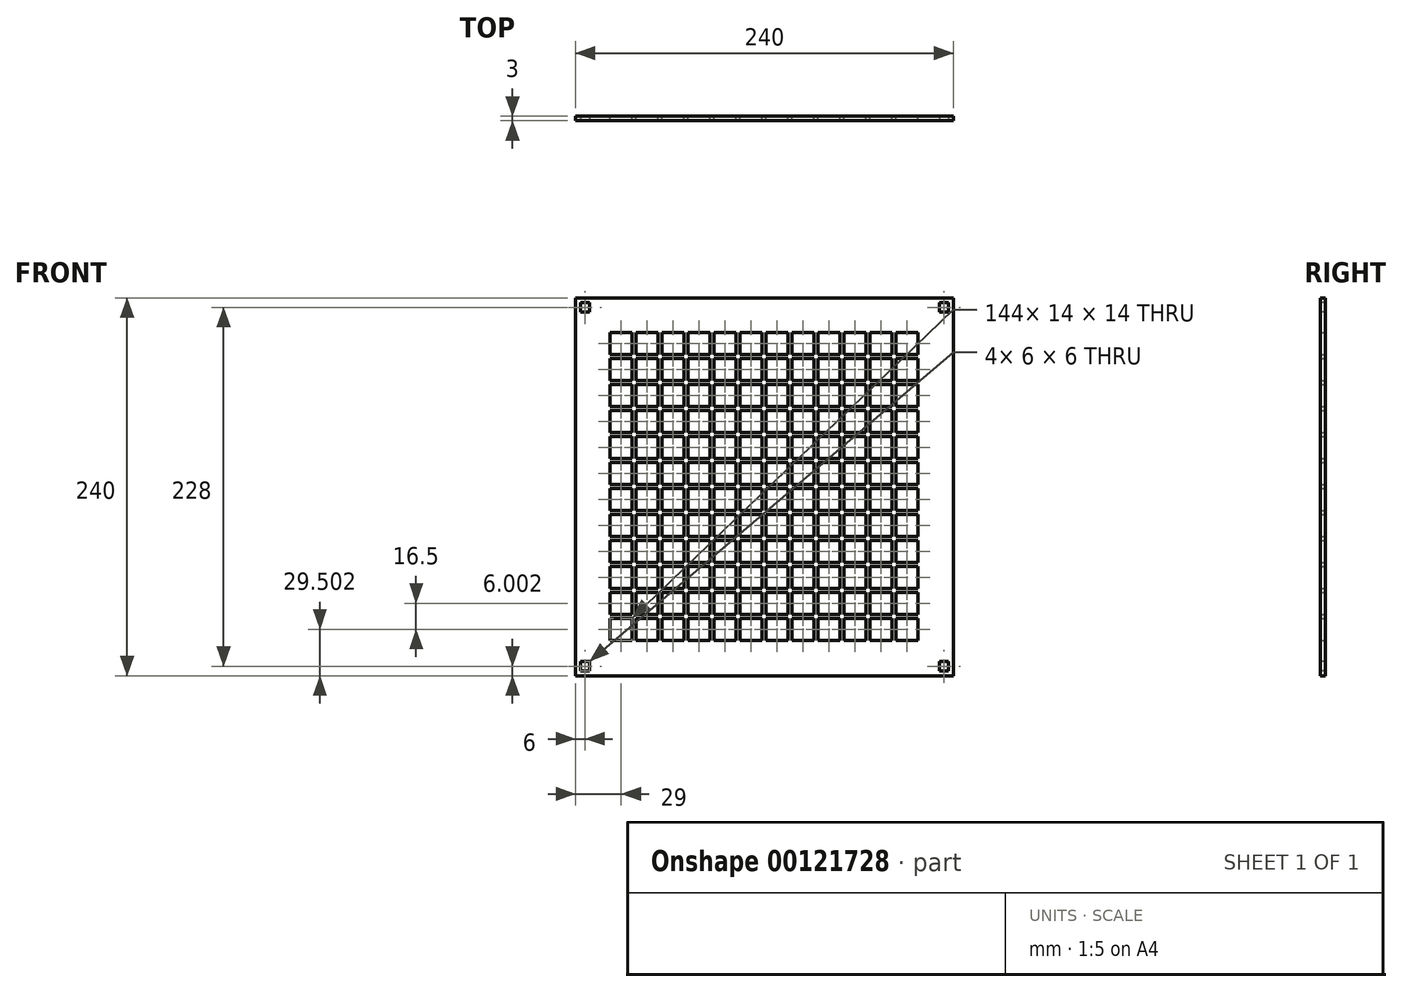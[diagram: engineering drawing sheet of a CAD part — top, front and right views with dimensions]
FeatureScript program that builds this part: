
annotation { "Feature Type Name" : "Feature", "Feature Type Description" : "" }
export const myFeature = defineFeature(function(context is Context, id is Id, definition is map)
    precondition{}
    {
        {
            var Q0;
            Q0=qCreatedBy(makeId("Front.planeOp"),FACE);
            var sketch = newSketch(context, id + "F0", { "sketchPlane" : qUnion([Q0])});
            skLineSegment(sketch, "E0.bottom", {"start": v(-132.55, 156.24) * mm, "end": v(107.45, 156.24) * mm});
            skLineSegment(sketch, "E0.top", {"start": v(-132.55, -83.76) * mm, "end": v(107.45, -83.76) * mm});
            skLineSegment(sketch, "E0.left", {"start": v(-132.55, 156.24) * mm, "end": v(-132.55, -83.76) * mm});
            skLineSegment(sketch, "E0.right", {"start": v(107.45, 156.24) * mm, "end": v(107.45, -83.76) * mm});
            skLineSegment(sketch, "E1.bottom", {"start": v(-110.55, 134.24) * mm, "end": v(-96.55, 134.24) * mm});
            skLineSegment(sketch, "E1.top", {"start": v(-110.55, 120.24) * mm, "end": v(-96.55, 120.24) * mm});
            skLineSegment(sketch, "E1.left", {"start": v(-110.55, 134.24) * mm, "end": v(-110.55, 120.24) * mm});
            skLineSegment(sketch, "E1.right", {"start": v(-96.55, 134.24) * mm, "end": v(-96.55, 120.24) * mm});
            skLineSegment(sketch, "E2.direction1", {"start": v(-110.55, 120.24) * mm, "end": v(-100.55, 120.24) * mm, "construction": true});
            skLineSegment(sketch, "E3.direction1", {"start": v(-110.55, 120.24) * mm, "end": v(-94.05, 120.24) * mm, "construction": true});
            skLineSegment(sketch, "E3.direction2", {"start": v(-110.55, 120.24) * mm, "end": v(-110.55, 87.24) * mm, "construction": true});
            skLineSegment(sketch, "E4.0.1.0", {"start": v(-94.05, 120.24) * mm, "end": v(-84.05, 120.24) * mm, "construction": true});
            skLineSegment(sketch, "E4.3.1.0", {"start": v(-80.05, 134.24) * mm, "end": v(-80.05, 120.24) * mm});
            skLineSegment(sketch, "E4.6.1.0", {"start": v(-94.05, 134.24) * mm, "end": v(-94.05, 120.24) * mm});
            skLineSegment(sketch, "E4.9.1.0", {"start": v(-94.05, 134.24) * mm, "end": v(-80.05, 134.24) * mm});
            skLineSegment(sketch, "E4.12.1.0", {"start": v(-94.05, 120.24) * mm, "end": v(-80.05, 120.24) * mm});
            skLineSegment(sketch, "E4.0.2.0", {"start": v(-77.55, 120.24) * mm, "end": v(-67.55, 120.24) * mm, "construction": true});
            skLineSegment(sketch, "E4.3.2.0", {"start": v(-63.55, 134.24) * mm, "end": v(-63.55, 120.24) * mm});
            skLineSegment(sketch, "E4.6.2.0", {"start": v(-77.55, 134.24) * mm, "end": v(-77.55, 120.24) * mm});
            skLineSegment(sketch, "E4.9.2.0", {"start": v(-77.55, 134.24) * mm, "end": v(-63.55, 134.24) * mm});
            skLineSegment(sketch, "E4.12.2.0", {"start": v(-77.55, 120.24) * mm, "end": v(-63.55, 120.24) * mm});
            skLineSegment(sketch, "E4.0.3.0", {"start": v(-61.05, 120.24) * mm, "end": v(-51.05, 120.24) * mm, "construction": true});
            skLineSegment(sketch, "E4.3.3.0", {"start": v(-47.05, 134.24) * mm, "end": v(-47.05, 120.24) * mm});
            skLineSegment(sketch, "E4.6.3.0", {"start": v(-61.05, 134.24) * mm, "end": v(-61.05, 120.24) * mm});
            skLineSegment(sketch, "E4.9.3.0", {"start": v(-61.05, 134.24) * mm, "end": v(-47.05, 134.24) * mm});
            skLineSegment(sketch, "E4.12.3.0", {"start": v(-61.05, 120.24) * mm, "end": v(-47.05, 120.24) * mm});
            skLineSegment(sketch, "E4.0.4.0", {"start": v(-44.55, 120.24) * mm, "end": v(-34.55, 120.24) * mm, "construction": true});
            skLineSegment(sketch, "E4.3.4.0", {"start": v(-30.55, 134.24) * mm, "end": v(-30.55, 120.24) * mm});
            skLineSegment(sketch, "E4.6.4.0", {"start": v(-44.55, 134.24) * mm, "end": v(-44.55, 120.24) * mm});
            skLineSegment(sketch, "E4.9.4.0", {"start": v(-44.55, 134.24) * mm, "end": v(-30.55, 134.24) * mm});
            skLineSegment(sketch, "E4.12.4.0", {"start": v(-44.55, 120.24) * mm, "end": v(-30.55, 120.24) * mm});
            skLineSegment(sketch, "E4.0.5.0", {"start": v(-28.05, 120.24) * mm, "end": v(-18.05, 120.24) * mm, "construction": true});
            skLineSegment(sketch, "E4.3.5.0", {"start": v(-14.05, 134.24) * mm, "end": v(-14.05, 120.24) * mm});
            skLineSegment(sketch, "E4.6.5.0", {"start": v(-28.05, 134.24) * mm, "end": v(-28.05, 120.24) * mm});
            skLineSegment(sketch, "E4.9.5.0", {"start": v(-28.05, 134.24) * mm, "end": v(-14.05, 134.24) * mm});
            skLineSegment(sketch, "E4.12.5.0", {"start": v(-28.05, 120.24) * mm, "end": v(-14.05, 120.24) * mm});
            skLineSegment(sketch, "E4.0.6.0", {"start": v(-11.55, 120.24) * mm, "end": v(-1.55, 120.24) * mm, "construction": true});
            skLineSegment(sketch, "E4.3.6.0", {"start": v(2.45, 134.24) * mm, "end": v(2.45, 120.24) * mm});
            skLineSegment(sketch, "E4.6.6.0", {"start": v(-11.55, 134.24) * mm, "end": v(-11.55, 120.24) * mm});
            skLineSegment(sketch, "E4.9.6.0", {"start": v(-11.55, 134.24) * mm, "end": v(2.45, 134.24) * mm});
            skLineSegment(sketch, "E4.12.6.0", {"start": v(-11.55, 120.24) * mm, "end": v(2.45, 120.24) * mm});
            skLineSegment(sketch, "E4.0.7.0", {"start": v(4.95, 120.24) * mm, "end": v(14.95, 120.24) * mm, "construction": true});
            skLineSegment(sketch, "E4.3.7.0", {"start": v(18.95, 134.24) * mm, "end": v(18.95, 120.24) * mm});
            skLineSegment(sketch, "E4.6.7.0", {"start": v(4.95, 134.24) * mm, "end": v(4.95, 120.24) * mm});
            skLineSegment(sketch, "E4.9.7.0", {"start": v(4.95, 134.24) * mm, "end": v(18.95, 134.24) * mm});
            skLineSegment(sketch, "E4.12.7.0", {"start": v(4.95, 120.24) * mm, "end": v(18.95, 120.24) * mm});
            skLineSegment(sketch, "E4.0.8.0", {"start": v(21.45, 120.24) * mm, "end": v(31.45, 120.24) * mm, "construction": true});
            skLineSegment(sketch, "E4.3.8.0", {"start": v(35.45, 134.24) * mm, "end": v(35.45, 120.24) * mm});
            skLineSegment(sketch, "E4.6.8.0", {"start": v(21.45, 134.24) * mm, "end": v(21.45, 120.24) * mm});
            skLineSegment(sketch, "E4.9.8.0", {"start": v(21.45, 134.24) * mm, "end": v(35.45, 134.24) * mm});
            skLineSegment(sketch, "E4.12.8.0", {"start": v(21.45, 120.24) * mm, "end": v(35.45, 120.24) * mm});
            skLineSegment(sketch, "E4.0.9.0", {"start": v(37.95, 120.24) * mm, "end": v(47.95, 120.24) * mm, "construction": true});
            skLineSegment(sketch, "E4.3.9.0", {"start": v(51.95, 134.24) * mm, "end": v(51.95, 120.24) * mm});
            skLineSegment(sketch, "E4.6.9.0", {"start": v(37.95, 134.24) * mm, "end": v(37.95, 120.24) * mm});
            skLineSegment(sketch, "E4.9.9.0", {"start": v(37.95, 134.24) * mm, "end": v(51.95, 134.24) * mm});
            skLineSegment(sketch, "E4.12.9.0", {"start": v(37.95, 120.24) * mm, "end": v(51.95, 120.24) * mm});
            skLineSegment(sketch, "E4.0.10.0", {"start": v(54.45, 120.24) * mm, "end": v(64.45, 120.24) * mm, "construction": true});
            skLineSegment(sketch, "E4.3.10.0", {"start": v(68.45, 134.24) * mm, "end": v(68.45, 120.24) * mm});
            skLineSegment(sketch, "E4.6.10.0", {"start": v(54.45, 134.24) * mm, "end": v(54.45, 120.24) * mm});
            skLineSegment(sketch, "E4.9.10.0", {"start": v(54.45, 134.24) * mm, "end": v(68.45, 134.24) * mm});
            skLineSegment(sketch, "E4.12.10.0", {"start": v(54.45, 120.24) * mm, "end": v(68.45, 120.24) * mm});
            skLineSegment(sketch, "E4.0.11.0", {"start": v(70.95, 120.24) * mm, "end": v(80.95, 120.24) * mm, "construction": true});
            skLineSegment(sketch, "E4.3.11.0", {"start": v(84.95, 134.24) * mm, "end": v(84.95, 120.24) * mm});
            skLineSegment(sketch, "E4.6.11.0", {"start": v(70.95, 134.24) * mm, "end": v(70.95, 120.24) * mm});
            skLineSegment(sketch, "E4.9.11.0", {"start": v(70.95, 134.24) * mm, "end": v(84.95, 134.24) * mm});
            skLineSegment(sketch, "E4.12.11.0", {"start": v(70.95, 120.24) * mm, "end": v(84.95, 120.24) * mm});
            skLineSegment(sketch, "E5.0.0.1", {"start": v(-110.55, 87.24) * mm, "end": v(-100.55, 87.24) * mm, "construction": true});
            skLineSegment(sketch, "E5.3.0.1", {"start": v(-96.55, 101.24) * mm, "end": v(-96.55, 87.24) * mm});
            skLineSegment(sketch, "E5.6.0.1", {"start": v(-110.55, 101.24) * mm, "end": v(-110.55, 87.24) * mm});
            skLineSegment(sketch, "E5.9.0.1", {"start": v(-110.55, 101.24) * mm, "end": v(-96.55, 101.24) * mm});
            skLineSegment(sketch, "E5.12.0.1", {"start": v(-110.55, 87.24) * mm, "end": v(-96.55, 87.24) * mm});
            skLineSegment(sketch, "E5.0.0.2", {"start": v(-110.55, 54.24) * mm, "end": v(-100.55, 54.24) * mm, "construction": true});
            skLineSegment(sketch, "E5.3.0.2", {"start": v(-96.55, 68.24) * mm, "end": v(-96.55, 54.24) * mm});
            skLineSegment(sketch, "E5.6.0.2", {"start": v(-110.55, 68.24) * mm, "end": v(-110.55, 54.24) * mm});
            skLineSegment(sketch, "E5.9.0.2", {"start": v(-110.55, 68.24) * mm, "end": v(-96.55, 68.24) * mm});
            skLineSegment(sketch, "E5.12.0.2", {"start": v(-110.55, 54.24) * mm, "end": v(-96.55, 54.24) * mm});
            skLineSegment(sketch, "E5.0.0.3", {"start": v(-110.55, 21.24) * mm, "end": v(-100.55, 21.24) * mm, "construction": true});
            skLineSegment(sketch, "E5.3.0.3", {"start": v(-96.55, 35.24) * mm, "end": v(-96.55, 21.24) * mm});
            skLineSegment(sketch, "E5.6.0.3", {"start": v(-110.55, 35.24) * mm, "end": v(-110.55, 21.24) * mm});
            skLineSegment(sketch, "E5.9.0.3", {"start": v(-110.55, 35.24) * mm, "end": v(-96.55, 35.24) * mm});
            skLineSegment(sketch, "E5.12.0.3", {"start": v(-110.55, 21.24) * mm, "end": v(-96.55, 21.24) * mm});
            skLineSegment(sketch, "E5.0.0.4", {"start": v(-110.55, -11.76) * mm, "end": v(-100.55, -11.76) * mm, "construction": true});
            skLineSegment(sketch, "E5.3.0.4", {"start": v(-96.55, 2.24) * mm, "end": v(-96.55, -11.76) * mm});
            skLineSegment(sketch, "E5.6.0.4", {"start": v(-110.55, 2.24) * mm, "end": v(-110.55, -11.76) * mm});
            skLineSegment(sketch, "E5.9.0.4", {"start": v(-110.55, 2.24) * mm, "end": v(-96.55, 2.24) * mm});
            skLineSegment(sketch, "E5.12.0.4", {"start": v(-110.55, -11.76) * mm, "end": v(-96.55, -11.76) * mm});
            skLineSegment(sketch, "E5.0.0.5", {"start": v(-110.55, -44.76) * mm, "end": v(-100.55, -44.76) * mm, "construction": true});
            skLineSegment(sketch, "E5.3.0.5", {"start": v(-96.55, -30.76) * mm, "end": v(-96.55, -44.76) * mm});
            skLineSegment(sketch, "E5.6.0.5", {"start": v(-110.55, -30.76) * mm, "end": v(-110.55, -44.76) * mm});
            skLineSegment(sketch, "E5.9.0.5", {"start": v(-110.55, -30.76) * mm, "end": v(-96.55, -30.76) * mm});
            skLineSegment(sketch, "E5.12.0.5", {"start": v(-110.55, -44.76) * mm, "end": v(-96.55, -44.76) * mm});
            skLineSegment(sketch, "E5.0.1.1", {"start": v(-94.05, 87.24) * mm, "end": v(-84.05, 87.24) * mm, "construction": true});
            skLineSegment(sketch, "E5.3.1.1", {"start": v(-80.05, 101.24) * mm, "end": v(-80.05, 87.24) * mm});
            skLineSegment(sketch, "E5.6.1.1", {"start": v(-94.05, 101.24) * mm, "end": v(-94.05, 87.24) * mm});
            skLineSegment(sketch, "E5.9.1.1", {"start": v(-94.05, 101.24) * mm, "end": v(-80.05, 101.24) * mm});
            skLineSegment(sketch, "E5.12.1.1", {"start": v(-94.05, 87.24) * mm, "end": v(-80.05, 87.24) * mm});
            skLineSegment(sketch, "E5.0.1.2", {"start": v(-94.05, 54.24) * mm, "end": v(-84.05, 54.24) * mm, "construction": true});
            skLineSegment(sketch, "E5.3.1.2", {"start": v(-80.05, 68.24) * mm, "end": v(-80.05, 54.24) * mm});
            skLineSegment(sketch, "E5.6.1.2", {"start": v(-94.05, 68.24) * mm, "end": v(-94.05, 54.24) * mm});
            skLineSegment(sketch, "E5.9.1.2", {"start": v(-94.05, 68.24) * mm, "end": v(-80.05, 68.24) * mm});
            skLineSegment(sketch, "E5.12.1.2", {"start": v(-94.05, 54.24) * mm, "end": v(-80.05, 54.24) * mm});
            skLineSegment(sketch, "E5.0.1.3", {"start": v(-94.05, 21.24) * mm, "end": v(-84.05, 21.24) * mm, "construction": true});
            skLineSegment(sketch, "E5.3.1.3", {"start": v(-80.05, 35.24) * mm, "end": v(-80.05, 21.24) * mm});
            skLineSegment(sketch, "E5.6.1.3", {"start": v(-94.05, 35.24) * mm, "end": v(-94.05, 21.24) * mm});
            skLineSegment(sketch, "E5.9.1.3", {"start": v(-94.05, 35.24) * mm, "end": v(-80.05, 35.24) * mm});
            skLineSegment(sketch, "E5.12.1.3", {"start": v(-94.05, 21.24) * mm, "end": v(-80.05, 21.24) * mm});
            skLineSegment(sketch, "E5.0.1.4", {"start": v(-94.05, -11.76) * mm, "end": v(-84.05, -11.76) * mm, "construction": true});
            skLineSegment(sketch, "E5.3.1.4", {"start": v(-80.05, 2.24) * mm, "end": v(-80.05, -11.76) * mm});
            skLineSegment(sketch, "E5.6.1.4", {"start": v(-94.05, 2.24) * mm, "end": v(-94.05, -11.76) * mm});
            skLineSegment(sketch, "E5.9.1.4", {"start": v(-94.05, 2.24) * mm, "end": v(-80.05, 2.24) * mm});
            skLineSegment(sketch, "E5.12.1.4", {"start": v(-94.05, -11.76) * mm, "end": v(-80.05, -11.76) * mm});
            skLineSegment(sketch, "E5.0.1.5", {"start": v(-94.05, -44.76) * mm, "end": v(-84.05, -44.76) * mm, "construction": true});
            skLineSegment(sketch, "E5.3.1.5", {"start": v(-80.05, -30.76) * mm, "end": v(-80.05, -44.76) * mm});
            skLineSegment(sketch, "E5.6.1.5", {"start": v(-94.05, -30.76) * mm, "end": v(-94.05, -44.76) * mm});
            skLineSegment(sketch, "E5.9.1.5", {"start": v(-94.05, -30.76) * mm, "end": v(-80.05, -30.76) * mm});
            skLineSegment(sketch, "E5.12.1.5", {"start": v(-94.05, -44.76) * mm, "end": v(-80.05, -44.76) * mm});
            skLineSegment(sketch, "E5.0.2.1", {"start": v(-77.55, 87.24) * mm, "end": v(-67.55, 87.24) * mm, "construction": true});
            skLineSegment(sketch, "E5.3.2.1", {"start": v(-63.55, 101.24) * mm, "end": v(-63.55, 87.24) * mm});
            skLineSegment(sketch, "E5.6.2.1", {"start": v(-77.55, 101.24) * mm, "end": v(-77.55, 87.24) * mm});
            skLineSegment(sketch, "E5.9.2.1", {"start": v(-77.55, 101.24) * mm, "end": v(-63.55, 101.24) * mm});
            skLineSegment(sketch, "E5.12.2.1", {"start": v(-77.55, 87.24) * mm, "end": v(-63.55, 87.24) * mm});
            skLineSegment(sketch, "E5.0.2.2", {"start": v(-77.55, 54.24) * mm, "end": v(-67.55, 54.24) * mm, "construction": true});
            skLineSegment(sketch, "E5.3.2.2", {"start": v(-63.55, 68.24) * mm, "end": v(-63.55, 54.24) * mm});
            skLineSegment(sketch, "E5.6.2.2", {"start": v(-77.55, 68.24) * mm, "end": v(-77.55, 54.24) * mm});
            skLineSegment(sketch, "E5.9.2.2", {"start": v(-77.55, 68.24) * mm, "end": v(-63.55, 68.24) * mm});
            skLineSegment(sketch, "E5.12.2.2", {"start": v(-77.55, 54.24) * mm, "end": v(-63.55, 54.24) * mm});
            skLineSegment(sketch, "E5.0.2.3", {"start": v(-77.55, 21.24) * mm, "end": v(-67.55, 21.24) * mm, "construction": true});
            skLineSegment(sketch, "E5.3.2.3", {"start": v(-63.55, 35.24) * mm, "end": v(-63.55, 21.24) * mm});
            skLineSegment(sketch, "E5.6.2.3", {"start": v(-77.55, 35.24) * mm, "end": v(-77.55, 21.24) * mm});
            skLineSegment(sketch, "E5.9.2.3", {"start": v(-77.55, 35.24) * mm, "end": v(-63.55, 35.24) * mm});
            skLineSegment(sketch, "E5.12.2.3", {"start": v(-77.55, 21.24) * mm, "end": v(-63.55, 21.24) * mm});
            skLineSegment(sketch, "E5.0.2.4", {"start": v(-77.55, -11.76) * mm, "end": v(-67.55, -11.76) * mm, "construction": true});
            skLineSegment(sketch, "E5.3.2.4", {"start": v(-63.55, 2.24) * mm, "end": v(-63.55, -11.76) * mm});
            skLineSegment(sketch, "E5.6.2.4", {"start": v(-77.55, 2.24) * mm, "end": v(-77.55, -11.76) * mm});
            skLineSegment(sketch, "E5.9.2.4", {"start": v(-77.55, 2.24) * mm, "end": v(-63.55, 2.24) * mm});
            skLineSegment(sketch, "E5.12.2.4", {"start": v(-77.55, -11.76) * mm, "end": v(-63.55, -11.76) * mm});
            skLineSegment(sketch, "E5.0.2.5", {"start": v(-77.55, -44.76) * mm, "end": v(-67.55, -44.76) * mm, "construction": true});
            skLineSegment(sketch, "E5.3.2.5", {"start": v(-63.55, -30.76) * mm, "end": v(-63.55, -44.76) * mm});
            skLineSegment(sketch, "E5.6.2.5", {"start": v(-77.55, -30.76) * mm, "end": v(-77.55, -44.76) * mm});
            skLineSegment(sketch, "E5.9.2.5", {"start": v(-77.55, -30.76) * mm, "end": v(-63.55, -30.76) * mm});
            skLineSegment(sketch, "E5.12.2.5", {"start": v(-77.55, -44.76) * mm, "end": v(-63.55, -44.76) * mm});
            skLineSegment(sketch, "E5.0.3.1", {"start": v(-61.05, 87.24) * mm, "end": v(-51.05, 87.24) * mm, "construction": true});
            skLineSegment(sketch, "E5.3.3.1", {"start": v(-47.05, 101.24) * mm, "end": v(-47.05, 87.24) * mm});
            skLineSegment(sketch, "E5.6.3.1", {"start": v(-61.05, 101.24) * mm, "end": v(-61.05, 87.24) * mm});
            skLineSegment(sketch, "E5.9.3.1", {"start": v(-61.05, 101.24) * mm, "end": v(-47.05, 101.24) * mm});
            skLineSegment(sketch, "E5.12.3.1", {"start": v(-61.05, 87.24) * mm, "end": v(-47.05, 87.24) * mm});
            skLineSegment(sketch, "E5.0.3.2", {"start": v(-61.05, 54.24) * mm, "end": v(-51.05, 54.24) * mm, "construction": true});
            skLineSegment(sketch, "E5.3.3.2", {"start": v(-47.05, 68.24) * mm, "end": v(-47.05, 54.24) * mm});
            skLineSegment(sketch, "E5.6.3.2", {"start": v(-61.05, 68.24) * mm, "end": v(-61.05, 54.24) * mm});
            skLineSegment(sketch, "E5.9.3.2", {"start": v(-61.05, 68.24) * mm, "end": v(-47.05, 68.24) * mm});
            skLineSegment(sketch, "E5.12.3.2", {"start": v(-61.05, 54.24) * mm, "end": v(-47.05, 54.24) * mm});
            skLineSegment(sketch, "E5.0.3.3", {"start": v(-61.05, 21.24) * mm, "end": v(-51.05, 21.24) * mm, "construction": true});
            skLineSegment(sketch, "E5.3.3.3", {"start": v(-47.05, 35.24) * mm, "end": v(-47.05, 21.24) * mm});
            skLineSegment(sketch, "E5.6.3.3", {"start": v(-61.05, 35.24) * mm, "end": v(-61.05, 21.24) * mm});
            skLineSegment(sketch, "E5.9.3.3", {"start": v(-61.05, 35.24) * mm, "end": v(-47.05, 35.24) * mm});
            skLineSegment(sketch, "E5.12.3.3", {"start": v(-61.05, 21.24) * mm, "end": v(-47.05, 21.24) * mm});
            skLineSegment(sketch, "E5.0.3.4", {"start": v(-61.05, -11.76) * mm, "end": v(-51.05, -11.76) * mm, "construction": true});
            skLineSegment(sketch, "E5.3.3.4", {"start": v(-47.05, 2.24) * mm, "end": v(-47.05, -11.76) * mm});
            skLineSegment(sketch, "E5.6.3.4", {"start": v(-61.05, 2.24) * mm, "end": v(-61.05, -11.76) * mm});
            skLineSegment(sketch, "E5.9.3.4", {"start": v(-61.05, 2.24) * mm, "end": v(-47.05, 2.24) * mm});
            skLineSegment(sketch, "E5.12.3.4", {"start": v(-61.05, -11.76) * mm, "end": v(-47.05, -11.76) * mm});
            skLineSegment(sketch, "E5.0.3.5", {"start": v(-61.05, -44.76) * mm, "end": v(-51.05, -44.76) * mm, "construction": true});
            skLineSegment(sketch, "E5.3.3.5", {"start": v(-47.05, -30.76) * mm, "end": v(-47.05, -44.76) * mm});
            skLineSegment(sketch, "E5.6.3.5", {"start": v(-61.05, -30.76) * mm, "end": v(-61.05, -44.76) * mm});
            skLineSegment(sketch, "E5.9.3.5", {"start": v(-61.05, -30.76) * mm, "end": v(-47.05, -30.76) * mm});
            skLineSegment(sketch, "E5.12.3.5", {"start": v(-61.05, -44.76) * mm, "end": v(-47.05, -44.76) * mm});
            skLineSegment(sketch, "E5.0.4.1", {"start": v(-44.55, 87.24) * mm, "end": v(-34.55, 87.24) * mm, "construction": true});
            skLineSegment(sketch, "E5.3.4.1", {"start": v(-30.55, 101.24) * mm, "end": v(-30.55, 87.24) * mm});
            skLineSegment(sketch, "E5.6.4.1", {"start": v(-44.55, 101.24) * mm, "end": v(-44.55, 87.24) * mm});
            skLineSegment(sketch, "E5.9.4.1", {"start": v(-44.55, 101.24) * mm, "end": v(-30.55, 101.24) * mm});
            skLineSegment(sketch, "E5.12.4.1", {"start": v(-44.55, 87.24) * mm, "end": v(-30.55, 87.24) * mm});
            skLineSegment(sketch, "E5.0.4.2", {"start": v(-44.55, 54.24) * mm, "end": v(-34.55, 54.24) * mm, "construction": true});
            skLineSegment(sketch, "E5.3.4.2", {"start": v(-30.55, 68.24) * mm, "end": v(-30.55, 54.24) * mm});
            skLineSegment(sketch, "E5.6.4.2", {"start": v(-44.55, 68.24) * mm, "end": v(-44.55, 54.24) * mm});
            skLineSegment(sketch, "E5.9.4.2", {"start": v(-44.55, 68.24) * mm, "end": v(-30.55, 68.24) * mm});
            skLineSegment(sketch, "E5.12.4.2", {"start": v(-44.55, 54.24) * mm, "end": v(-30.55, 54.24) * mm});
            skLineSegment(sketch, "E5.0.4.3", {"start": v(-44.55, 21.24) * mm, "end": v(-34.55, 21.24) * mm, "construction": true});
            skLineSegment(sketch, "E5.3.4.3", {"start": v(-30.55, 35.24) * mm, "end": v(-30.55, 21.24) * mm});
            skLineSegment(sketch, "E5.6.4.3", {"start": v(-44.55, 35.24) * mm, "end": v(-44.55, 21.24) * mm});
            skLineSegment(sketch, "E5.9.4.3", {"start": v(-44.55, 35.24) * mm, "end": v(-30.55, 35.24) * mm});
            skLineSegment(sketch, "E5.12.4.3", {"start": v(-44.55, 21.24) * mm, "end": v(-30.55, 21.24) * mm});
            skLineSegment(sketch, "E5.0.4.4", {"start": v(-44.55, -11.76) * mm, "end": v(-34.55, -11.76) * mm, "construction": true});
            skLineSegment(sketch, "E5.3.4.4", {"start": v(-30.55, 2.24) * mm, "end": v(-30.55, -11.76) * mm});
            skLineSegment(sketch, "E5.6.4.4", {"start": v(-44.55, 2.24) * mm, "end": v(-44.55, -11.76) * mm});
            skLineSegment(sketch, "E5.9.4.4", {"start": v(-44.55, 2.24) * mm, "end": v(-30.55, 2.24) * mm});
            skLineSegment(sketch, "E5.12.4.4", {"start": v(-44.55, -11.76) * mm, "end": v(-30.55, -11.76) * mm});
            skLineSegment(sketch, "E5.0.4.5", {"start": v(-44.55, -44.76) * mm, "end": v(-34.55, -44.76) * mm, "construction": true});
            skLineSegment(sketch, "E5.3.4.5", {"start": v(-30.55, -30.76) * mm, "end": v(-30.55, -44.76) * mm});
            skLineSegment(sketch, "E5.6.4.5", {"start": v(-44.55, -30.76) * mm, "end": v(-44.55, -44.76) * mm});
            skLineSegment(sketch, "E5.9.4.5", {"start": v(-44.55, -30.76) * mm, "end": v(-30.55, -30.76) * mm});
            skLineSegment(sketch, "E5.12.4.5", {"start": v(-44.55, -44.76) * mm, "end": v(-30.55, -44.76) * mm});
            skLineSegment(sketch, "E5.0.5.1", {"start": v(-28.05, 87.24) * mm, "end": v(-18.05, 87.24) * mm, "construction": true});
            skLineSegment(sketch, "E5.3.5.1", {"start": v(-14.05, 101.24) * mm, "end": v(-14.05, 87.24) * mm});
            skLineSegment(sketch, "E5.6.5.1", {"start": v(-28.05, 101.24) * mm, "end": v(-28.05, 87.24) * mm});
            skLineSegment(sketch, "E5.9.5.1", {"start": v(-28.05, 101.24) * mm, "end": v(-14.05, 101.24) * mm});
            skLineSegment(sketch, "E5.12.5.1", {"start": v(-28.05, 87.24) * mm, "end": v(-14.05, 87.24) * mm});
            skLineSegment(sketch, "E5.0.5.2", {"start": v(-28.05, 54.24) * mm, "end": v(-18.05, 54.24) * mm, "construction": true});
            skLineSegment(sketch, "E5.3.5.2", {"start": v(-14.05, 68.24) * mm, "end": v(-14.05, 54.24) * mm});
            skLineSegment(sketch, "E5.6.5.2", {"start": v(-28.05, 68.24) * mm, "end": v(-28.05, 54.24) * mm});
            skLineSegment(sketch, "E5.9.5.2", {"start": v(-28.05, 68.24) * mm, "end": v(-14.05, 68.24) * mm});
            skLineSegment(sketch, "E5.12.5.2", {"start": v(-28.05, 54.24) * mm, "end": v(-14.05, 54.24) * mm});
            skLineSegment(sketch, "E5.0.5.3", {"start": v(-28.05, 21.24) * mm, "end": v(-18.05, 21.24) * mm, "construction": true});
            skLineSegment(sketch, "E5.3.5.3", {"start": v(-14.05, 35.24) * mm, "end": v(-14.05, 21.24) * mm});
            skLineSegment(sketch, "E5.6.5.3", {"start": v(-28.05, 35.24) * mm, "end": v(-28.05, 21.24) * mm});
            skLineSegment(sketch, "E5.9.5.3", {"start": v(-28.05, 35.24) * mm, "end": v(-14.05, 35.24) * mm});
            skLineSegment(sketch, "E5.12.5.3", {"start": v(-28.05, 21.24) * mm, "end": v(-14.05, 21.24) * mm});
            skLineSegment(sketch, "E5.0.5.4", {"start": v(-28.05, -11.76) * mm, "end": v(-18.05, -11.76) * mm, "construction": true});
            skLineSegment(sketch, "E5.3.5.4", {"start": v(-14.05, 2.24) * mm, "end": v(-14.05, -11.76) * mm});
            skLineSegment(sketch, "E5.6.5.4", {"start": v(-28.05, 2.24) * mm, "end": v(-28.05, -11.76) * mm});
            skLineSegment(sketch, "E5.9.5.4", {"start": v(-28.05, 2.24) * mm, "end": v(-14.05, 2.24) * mm});
            skLineSegment(sketch, "E5.12.5.4", {"start": v(-28.05, -11.76) * mm, "end": v(-14.05, -11.76) * mm});
            skLineSegment(sketch, "E5.0.5.5", {"start": v(-28.05, -44.76) * mm, "end": v(-18.05, -44.76) * mm, "construction": true});
            skLineSegment(sketch, "E5.3.5.5", {"start": v(-14.05, -30.76) * mm, "end": v(-14.05, -44.76) * mm});
            skLineSegment(sketch, "E5.6.5.5", {"start": v(-28.05, -30.76) * mm, "end": v(-28.05, -44.76) * mm});
            skLineSegment(sketch, "E5.9.5.5", {"start": v(-28.05, -30.76) * mm, "end": v(-14.05, -30.76) * mm});
            skLineSegment(sketch, "E5.12.5.5", {"start": v(-28.05, -44.76) * mm, "end": v(-14.05, -44.76) * mm});
            skLineSegment(sketch, "E5.0.6.1", {"start": v(-11.55, 87.24) * mm, "end": v(-1.55, 87.24) * mm, "construction": true});
            skLineSegment(sketch, "E5.3.6.1", {"start": v(2.45, 101.24) * mm, "end": v(2.45, 87.24) * mm});
            skLineSegment(sketch, "E5.6.6.1", {"start": v(-11.55, 101.24) * mm, "end": v(-11.55, 87.24) * mm});
            skLineSegment(sketch, "E5.9.6.1", {"start": v(-11.55, 101.24) * mm, "end": v(2.45, 101.24) * mm});
            skLineSegment(sketch, "E5.12.6.1", {"start": v(-11.55, 87.24) * mm, "end": v(2.45, 87.24) * mm});
            skLineSegment(sketch, "E5.0.6.2", {"start": v(-11.55, 54.24) * mm, "end": v(-1.55, 54.24) * mm, "construction": true});
            skLineSegment(sketch, "E5.3.6.2", {"start": v(2.45, 68.24) * mm, "end": v(2.45, 54.24) * mm});
            skLineSegment(sketch, "E5.6.6.2", {"start": v(-11.55, 68.24) * mm, "end": v(-11.55, 54.24) * mm});
            skLineSegment(sketch, "E5.9.6.2", {"start": v(-11.55, 68.24) * mm, "end": v(2.45, 68.24) * mm});
            skLineSegment(sketch, "E5.12.6.2", {"start": v(-11.55, 54.24) * mm, "end": v(2.45, 54.24) * mm});
            skLineSegment(sketch, "E5.0.6.3", {"start": v(-11.55, 21.24) * mm, "end": v(-1.55, 21.24) * mm, "construction": true});
            skLineSegment(sketch, "E5.3.6.3", {"start": v(2.45, 35.24) * mm, "end": v(2.45, 21.24) * mm});
            skLineSegment(sketch, "E5.6.6.3", {"start": v(-11.55, 35.24) * mm, "end": v(-11.55, 21.24) * mm});
            skLineSegment(sketch, "E5.9.6.3", {"start": v(-11.55, 35.24) * mm, "end": v(2.45, 35.24) * mm});
            skLineSegment(sketch, "E5.12.6.3", {"start": v(-11.55, 21.24) * mm, "end": v(2.45, 21.24) * mm});
            skLineSegment(sketch, "E5.0.6.4", {"start": v(-11.55, -11.76) * mm, "end": v(-1.55, -11.76) * mm, "construction": true});
            skLineSegment(sketch, "E5.3.6.4", {"start": v(2.45, 2.24) * mm, "end": v(2.45, -11.76) * mm});
            skLineSegment(sketch, "E5.6.6.4", {"start": v(-11.55, 2.24) * mm, "end": v(-11.55, -11.76) * mm});
            skLineSegment(sketch, "E5.9.6.4", {"start": v(-11.55, 2.24) * mm, "end": v(2.45, 2.24) * mm});
            skLineSegment(sketch, "E5.12.6.4", {"start": v(-11.55, -11.76) * mm, "end": v(2.45, -11.76) * mm});
            skLineSegment(sketch, "E5.0.6.5", {"start": v(-11.55, -44.76) * mm, "end": v(-1.55, -44.76) * mm, "construction": true});
            skLineSegment(sketch, "E5.3.6.5", {"start": v(2.45, -30.76) * mm, "end": v(2.45, -44.76) * mm});
            skLineSegment(sketch, "E5.6.6.5", {"start": v(-11.55, -30.76) * mm, "end": v(-11.55, -44.76) * mm});
            skLineSegment(sketch, "E5.9.6.5", {"start": v(-11.55, -30.76) * mm, "end": v(2.45, -30.76) * mm});
            skLineSegment(sketch, "E5.12.6.5", {"start": v(-11.55, -44.76) * mm, "end": v(2.45, -44.76) * mm});
            skLineSegment(sketch, "E5.0.7.1", {"start": v(4.95, 87.24) * mm, "end": v(14.95, 87.24) * mm, "construction": true});
            skLineSegment(sketch, "E5.3.7.1", {"start": v(18.95, 101.24) * mm, "end": v(18.95, 87.24) * mm});
            skLineSegment(sketch, "E5.6.7.1", {"start": v(4.95, 101.24) * mm, "end": v(4.95, 87.24) * mm});
            skLineSegment(sketch, "E5.9.7.1", {"start": v(4.95, 101.24) * mm, "end": v(18.95, 101.24) * mm});
            skLineSegment(sketch, "E5.12.7.1", {"start": v(4.95, 87.24) * mm, "end": v(18.95, 87.24) * mm});
            skLineSegment(sketch, "E5.0.7.2", {"start": v(4.95, 54.24) * mm, "end": v(14.95, 54.24) * mm, "construction": true});
            skLineSegment(sketch, "E5.3.7.2", {"start": v(18.95, 68.24) * mm, "end": v(18.95, 54.24) * mm});
            skLineSegment(sketch, "E5.6.7.2", {"start": v(4.95, 68.24) * mm, "end": v(4.95, 54.24) * mm});
            skLineSegment(sketch, "E5.9.7.2", {"start": v(4.95, 68.24) * mm, "end": v(18.95, 68.24) * mm});
            skLineSegment(sketch, "E5.12.7.2", {"start": v(4.95, 54.24) * mm, "end": v(18.95, 54.24) * mm});
            skLineSegment(sketch, "E5.0.7.3", {"start": v(4.95, 21.24) * mm, "end": v(14.95, 21.24) * mm, "construction": true});
            skLineSegment(sketch, "E5.3.7.3", {"start": v(18.95, 35.24) * mm, "end": v(18.95, 21.24) * mm});
            skLineSegment(sketch, "E5.6.7.3", {"start": v(4.95, 35.24) * mm, "end": v(4.95, 21.24) * mm});
            skLineSegment(sketch, "E5.9.7.3", {"start": v(4.95, 35.24) * mm, "end": v(18.95, 35.24) * mm});
            skLineSegment(sketch, "E5.12.7.3", {"start": v(4.95, 21.24) * mm, "end": v(18.95, 21.24) * mm});
            skLineSegment(sketch, "E5.0.7.4", {"start": v(4.95, -11.76) * mm, "end": v(14.95, -11.76) * mm, "construction": true});
            skLineSegment(sketch, "E5.3.7.4", {"start": v(18.95, 2.24) * mm, "end": v(18.95, -11.76) * mm});
            skLineSegment(sketch, "E5.6.7.4", {"start": v(4.95, 2.24) * mm, "end": v(4.95, -11.76) * mm});
            skLineSegment(sketch, "E5.9.7.4", {"start": v(4.95, 2.24) * mm, "end": v(18.95, 2.24) * mm});
            skLineSegment(sketch, "E5.12.7.4", {"start": v(4.95, -11.76) * mm, "end": v(18.95, -11.76) * mm});
            skLineSegment(sketch, "E5.0.7.5", {"start": v(4.95, -44.76) * mm, "end": v(14.95, -44.76) * mm, "construction": true});
            skLineSegment(sketch, "E5.3.7.5", {"start": v(18.95, -30.76) * mm, "end": v(18.95, -44.76) * mm});
            skLineSegment(sketch, "E5.6.7.5", {"start": v(4.95, -30.76) * mm, "end": v(4.95, -44.76) * mm});
            skLineSegment(sketch, "E5.9.7.5", {"start": v(4.95, -30.76) * mm, "end": v(18.95, -30.76) * mm});
            skLineSegment(sketch, "E5.12.7.5", {"start": v(4.95, -44.76) * mm, "end": v(18.95, -44.76) * mm});
            skLineSegment(sketch, "E5.0.8.1", {"start": v(21.45, 87.24) * mm, "end": v(31.45, 87.24) * mm, "construction": true});
            skLineSegment(sketch, "E5.3.8.1", {"start": v(35.45, 101.24) * mm, "end": v(35.45, 87.24) * mm});
            skLineSegment(sketch, "E5.6.8.1", {"start": v(21.45, 101.24) * mm, "end": v(21.45, 87.24) * mm});
            skLineSegment(sketch, "E5.9.8.1", {"start": v(21.45, 101.24) * mm, "end": v(35.45, 101.24) * mm});
            skLineSegment(sketch, "E5.12.8.1", {"start": v(21.45, 87.24) * mm, "end": v(35.45, 87.24) * mm});
            skLineSegment(sketch, "E5.0.8.2", {"start": v(21.45, 54.24) * mm, "end": v(31.45, 54.24) * mm, "construction": true});
            skLineSegment(sketch, "E5.3.8.2", {"start": v(35.45, 68.24) * mm, "end": v(35.45, 54.24) * mm});
            skLineSegment(sketch, "E5.6.8.2", {"start": v(21.45, 68.24) * mm, "end": v(21.45, 54.24) * mm});
            skLineSegment(sketch, "E5.9.8.2", {"start": v(21.45, 68.24) * mm, "end": v(35.45, 68.24) * mm});
            skLineSegment(sketch, "E5.12.8.2", {"start": v(21.45, 54.24) * mm, "end": v(35.45, 54.24) * mm});
            skLineSegment(sketch, "E5.0.8.3", {"start": v(21.45, 21.24) * mm, "end": v(31.45, 21.24) * mm, "construction": true});
            skLineSegment(sketch, "E5.3.8.3", {"start": v(35.45, 35.24) * mm, "end": v(35.45, 21.24) * mm});
            skLineSegment(sketch, "E5.6.8.3", {"start": v(21.45, 35.24) * mm, "end": v(21.45, 21.24) * mm});
            skLineSegment(sketch, "E5.9.8.3", {"start": v(21.45, 35.24) * mm, "end": v(35.45, 35.24) * mm});
            skLineSegment(sketch, "E5.12.8.3", {"start": v(21.45, 21.24) * mm, "end": v(35.45, 21.24) * mm});
            skLineSegment(sketch, "E5.0.8.4", {"start": v(21.45, -11.76) * mm, "end": v(31.45, -11.76) * mm, "construction": true});
            skLineSegment(sketch, "E5.3.8.4", {"start": v(35.45, 2.24) * mm, "end": v(35.45, -11.76) * mm});
            skLineSegment(sketch, "E5.6.8.4", {"start": v(21.45, 2.24) * mm, "end": v(21.45, -11.76) * mm});
            skLineSegment(sketch, "E5.9.8.4", {"start": v(21.45, 2.24) * mm, "end": v(35.45, 2.24) * mm});
            skLineSegment(sketch, "E5.12.8.4", {"start": v(21.45, -11.76) * mm, "end": v(35.45, -11.76) * mm});
            skLineSegment(sketch, "E5.0.8.5", {"start": v(21.45, -44.76) * mm, "end": v(31.45, -44.76) * mm, "construction": true});
            skLineSegment(sketch, "E5.3.8.5", {"start": v(35.45, -30.76) * mm, "end": v(35.45, -44.76) * mm});
            skLineSegment(sketch, "E5.6.8.5", {"start": v(21.45, -30.76) * mm, "end": v(21.45, -44.76) * mm});
            skLineSegment(sketch, "E5.9.8.5", {"start": v(21.45, -30.76) * mm, "end": v(35.45, -30.76) * mm});
            skLineSegment(sketch, "E5.12.8.5", {"start": v(21.45, -44.76) * mm, "end": v(35.45, -44.76) * mm});
            skLineSegment(sketch, "E5.0.9.1", {"start": v(37.95, 87.24) * mm, "end": v(47.95, 87.24) * mm, "construction": true});
            skLineSegment(sketch, "E5.3.9.1", {"start": v(51.95, 101.24) * mm, "end": v(51.95, 87.24) * mm});
            skLineSegment(sketch, "E5.6.9.1", {"start": v(37.95, 101.24) * mm, "end": v(37.95, 87.24) * mm});
            skLineSegment(sketch, "E5.9.9.1", {"start": v(37.95, 101.24) * mm, "end": v(51.95, 101.24) * mm});
            skLineSegment(sketch, "E5.12.9.1", {"start": v(37.95, 87.24) * mm, "end": v(51.95, 87.24) * mm});
            skLineSegment(sketch, "E5.0.9.2", {"start": v(37.95, 54.24) * mm, "end": v(47.95, 54.24) * mm, "construction": true});
            skLineSegment(sketch, "E5.3.9.2", {"start": v(51.95, 68.24) * mm, "end": v(51.95, 54.24) * mm});
            skLineSegment(sketch, "E5.6.9.2", {"start": v(37.95, 68.24) * mm, "end": v(37.95, 54.24) * mm});
            skLineSegment(sketch, "E5.9.9.2", {"start": v(37.95, 68.24) * mm, "end": v(51.95, 68.24) * mm});
            skLineSegment(sketch, "E5.12.9.2", {"start": v(37.95, 54.24) * mm, "end": v(51.95, 54.24) * mm});
            skLineSegment(sketch, "E5.0.9.3", {"start": v(37.95, 21.24) * mm, "end": v(47.95, 21.24) * mm, "construction": true});
            skLineSegment(sketch, "E5.3.9.3", {"start": v(51.95, 35.24) * mm, "end": v(51.95, 21.24) * mm});
            skLineSegment(sketch, "E5.6.9.3", {"start": v(37.95, 35.24) * mm, "end": v(37.95, 21.24) * mm});
            skLineSegment(sketch, "E5.9.9.3", {"start": v(37.95, 35.24) * mm, "end": v(51.95, 35.24) * mm});
            skLineSegment(sketch, "E5.12.9.3", {"start": v(37.95, 21.24) * mm, "end": v(51.95, 21.24) * mm});
            skLineSegment(sketch, "E5.0.9.4", {"start": v(37.95, -11.76) * mm, "end": v(47.95, -11.76) * mm, "construction": true});
            skLineSegment(sketch, "E5.3.9.4", {"start": v(51.95, 2.24) * mm, "end": v(51.95, -11.76) * mm});
            skLineSegment(sketch, "E5.6.9.4", {"start": v(37.95, 2.24) * mm, "end": v(37.95, -11.76) * mm});
            skLineSegment(sketch, "E5.9.9.4", {"start": v(37.95, 2.24) * mm, "end": v(51.95, 2.24) * mm});
            skLineSegment(sketch, "E5.12.9.4", {"start": v(37.95, -11.76) * mm, "end": v(51.95, -11.76) * mm});
            skLineSegment(sketch, "E5.0.9.5", {"start": v(37.95, -44.76) * mm, "end": v(47.95, -44.76) * mm, "construction": true});
            skLineSegment(sketch, "E5.3.9.5", {"start": v(51.95, -30.76) * mm, "end": v(51.95, -44.76) * mm});
            skLineSegment(sketch, "E5.6.9.5", {"start": v(37.95, -30.76) * mm, "end": v(37.95, -44.76) * mm});
            skLineSegment(sketch, "E5.9.9.5", {"start": v(37.95, -30.76) * mm, "end": v(51.95, -30.76) * mm});
            skLineSegment(sketch, "E5.12.9.5", {"start": v(37.95, -44.76) * mm, "end": v(51.95, -44.76) * mm});
            skLineSegment(sketch, "E5.0.10.1", {"start": v(54.45, 87.24) * mm, "end": v(64.45, 87.24) * mm, "construction": true});
            skLineSegment(sketch, "E5.3.10.1", {"start": v(68.45, 101.24) * mm, "end": v(68.45, 87.24) * mm});
            skLineSegment(sketch, "E5.6.10.1", {"start": v(54.45, 101.24) * mm, "end": v(54.45, 87.24) * mm});
            skLineSegment(sketch, "E5.9.10.1", {"start": v(54.45, 101.24) * mm, "end": v(68.45, 101.24) * mm});
            skLineSegment(sketch, "E5.12.10.1", {"start": v(54.45, 87.24) * mm, "end": v(68.45, 87.24) * mm});
            skLineSegment(sketch, "E5.0.10.2", {"start": v(54.45, 54.24) * mm, "end": v(64.45, 54.24) * mm, "construction": true});
            skLineSegment(sketch, "E5.3.10.2", {"start": v(68.45, 68.24) * mm, "end": v(68.45, 54.24) * mm});
            skLineSegment(sketch, "E5.6.10.2", {"start": v(54.45, 68.24) * mm, "end": v(54.45, 54.24) * mm});
            skLineSegment(sketch, "E5.9.10.2", {"start": v(54.45, 68.24) * mm, "end": v(68.45, 68.24) * mm});
            skLineSegment(sketch, "E5.12.10.2", {"start": v(54.45, 54.24) * mm, "end": v(68.45, 54.24) * mm});
            skLineSegment(sketch, "E5.0.10.3", {"start": v(54.45, 21.24) * mm, "end": v(64.45, 21.24) * mm, "construction": true});
            skLineSegment(sketch, "E5.3.10.3", {"start": v(68.45, 35.24) * mm, "end": v(68.45, 21.24) * mm});
            skLineSegment(sketch, "E5.6.10.3", {"start": v(54.45, 35.24) * mm, "end": v(54.45, 21.24) * mm});
            skLineSegment(sketch, "E5.9.10.3", {"start": v(54.45, 35.24) * mm, "end": v(68.45, 35.24) * mm});
            skLineSegment(sketch, "E5.12.10.3", {"start": v(54.45, 21.24) * mm, "end": v(68.45, 21.24) * mm});
            skLineSegment(sketch, "E5.0.10.4", {"start": v(54.45, -11.76) * mm, "end": v(64.45, -11.76) * mm, "construction": true});
            skLineSegment(sketch, "E5.3.10.4", {"start": v(68.45, 2.24) * mm, "end": v(68.45, -11.76) * mm});
            skLineSegment(sketch, "E5.6.10.4", {"start": v(54.45, 2.24) * mm, "end": v(54.45, -11.76) * mm});
            skLineSegment(sketch, "E5.9.10.4", {"start": v(54.45, 2.24) * mm, "end": v(68.45, 2.24) * mm});
            skLineSegment(sketch, "E5.12.10.4", {"start": v(54.45, -11.76) * mm, "end": v(68.45, -11.76) * mm});
            skLineSegment(sketch, "E5.0.10.5", {"start": v(54.45, -44.76) * mm, "end": v(64.45, -44.76) * mm, "construction": true});
            skLineSegment(sketch, "E5.3.10.5", {"start": v(68.45, -30.76) * mm, "end": v(68.45, -44.76) * mm});
            skLineSegment(sketch, "E5.6.10.5", {"start": v(54.45, -30.76) * mm, "end": v(54.45, -44.76) * mm});
            skLineSegment(sketch, "E5.9.10.5", {"start": v(54.45, -30.76) * mm, "end": v(68.45, -30.76) * mm});
            skLineSegment(sketch, "E5.12.10.5", {"start": v(54.45, -44.76) * mm, "end": v(68.45, -44.76) * mm});
            skLineSegment(sketch, "E5.0.11.1", {"start": v(70.95, 87.24) * mm, "end": v(80.95, 87.24) * mm, "construction": true});
            skLineSegment(sketch, "E5.3.11.1", {"start": v(84.95, 101.24) * mm, "end": v(84.95, 87.24) * mm});
            skLineSegment(sketch, "E5.6.11.1", {"start": v(70.95, 101.24) * mm, "end": v(70.95, 87.24) * mm});
            skLineSegment(sketch, "E5.9.11.1", {"start": v(70.95, 101.24) * mm, "end": v(84.95, 101.24) * mm});
            skLineSegment(sketch, "E5.12.11.1", {"start": v(70.95, 87.24) * mm, "end": v(84.95, 87.24) * mm});
            skLineSegment(sketch, "E5.0.11.2", {"start": v(70.95, 54.24) * mm, "end": v(80.95, 54.24) * mm, "construction": true});
            skLineSegment(sketch, "E5.3.11.2", {"start": v(84.95, 68.24) * mm, "end": v(84.95, 54.24) * mm});
            skLineSegment(sketch, "E5.6.11.2", {"start": v(70.95, 68.24) * mm, "end": v(70.95, 54.24) * mm});
            skLineSegment(sketch, "E5.9.11.2", {"start": v(70.95, 68.24) * mm, "end": v(84.95, 68.24) * mm});
            skLineSegment(sketch, "E5.12.11.2", {"start": v(70.95, 54.24) * mm, "end": v(84.95, 54.24) * mm});
            skLineSegment(sketch, "E5.0.11.3", {"start": v(70.95, 21.24) * mm, "end": v(80.95, 21.24) * mm, "construction": true});
            skLineSegment(sketch, "E5.3.11.3", {"start": v(84.95, 35.24) * mm, "end": v(84.95, 21.24) * mm});
            skLineSegment(sketch, "E5.6.11.3", {"start": v(70.95, 35.24) * mm, "end": v(70.95, 21.24) * mm});
            skLineSegment(sketch, "E5.9.11.3", {"start": v(70.95, 35.24) * mm, "end": v(84.95, 35.24) * mm});
            skLineSegment(sketch, "E5.12.11.3", {"start": v(70.95, 21.24) * mm, "end": v(84.95, 21.24) * mm});
            skLineSegment(sketch, "E5.0.11.4", {"start": v(70.95, -11.76) * mm, "end": v(80.95, -11.76) * mm, "construction": true});
            skLineSegment(sketch, "E5.3.11.4", {"start": v(84.95, 2.24) * mm, "end": v(84.95, -11.76) * mm});
            skLineSegment(sketch, "E5.6.11.4", {"start": v(70.95, 2.24) * mm, "end": v(70.95, -11.76) * mm});
            skLineSegment(sketch, "E5.9.11.4", {"start": v(70.95, 2.24) * mm, "end": v(84.95, 2.24) * mm});
            skLineSegment(sketch, "E5.12.11.4", {"start": v(70.95, -11.76) * mm, "end": v(84.95, -11.76) * mm});
            skLineSegment(sketch, "E5.0.11.5", {"start": v(70.95, -44.76) * mm, "end": v(80.95, -44.76) * mm, "construction": true});
            skLineSegment(sketch, "E5.3.11.5", {"start": v(84.95, -30.76) * mm, "end": v(84.95, -44.76) * mm});
            skLineSegment(sketch, "E5.6.11.5", {"start": v(70.95, -30.76) * mm, "end": v(70.95, -44.76) * mm});
            skLineSegment(sketch, "E5.9.11.5", {"start": v(70.95, -30.76) * mm, "end": v(84.95, -30.76) * mm});
            skLineSegment(sketch, "E5.12.11.5", {"start": v(70.95, -44.76) * mm, "end": v(84.95, -44.76) * mm});
            skLineSegment(sketch, "E6.bottom", {"start": v(-110.55, 117.74) * mm, "end": v(-96.55, 117.74) * mm});
            skLineSegment(sketch, "E6.top", {"start": v(-110.55, 103.74) * mm, "end": v(-96.55, 103.74) * mm});
            skLineSegment(sketch, "E6.left", {"start": v(-110.55, 117.74) * mm, "end": v(-110.55, 103.74) * mm});
            skLineSegment(sketch, "E6.right", {"start": v(-96.55, 117.74) * mm, "end": v(-96.55, 103.74) * mm});
            skLineSegment(sketch, "E7.0.1.0", {"start": v(-110.55, 84.74) * mm, "end": v(-96.55, 84.74) * mm});
            skLineSegment(sketch, "E7.0.1.1", {"start": v(-96.55, 84.74) * mm, "end": v(-96.55, 70.74) * mm});
            skLineSegment(sketch, "E7.0.1.2", {"start": v(-110.55, 70.74) * mm, "end": v(-96.55, 70.74) * mm});
            skLineSegment(sketch, "E7.0.1.3", {"start": v(-110.55, 84.74) * mm, "end": v(-110.55, 70.74) * mm});
            skLineSegment(sketch, "E7.0.2.0", {"start": v(-110.55, 51.74) * mm, "end": v(-96.55, 51.74) * mm});
            skLineSegment(sketch, "E7.0.2.1", {"start": v(-96.55, 51.74) * mm, "end": v(-96.55, 37.74) * mm});
            skLineSegment(sketch, "E7.0.2.2", {"start": v(-110.55, 37.74) * mm, "end": v(-96.55, 37.74) * mm});
            skLineSegment(sketch, "E7.0.2.3", {"start": v(-110.55, 51.74) * mm, "end": v(-110.55, 37.74) * mm});
            skLineSegment(sketch, "E7.0.3.0", {"start": v(-110.55, 18.74) * mm, "end": v(-96.55, 18.74) * mm});
            skLineSegment(sketch, "E7.0.3.1", {"start": v(-96.55, 18.74) * mm, "end": v(-96.55, 4.74) * mm});
            skLineSegment(sketch, "E7.0.3.2", {"start": v(-110.55, 4.74) * mm, "end": v(-96.55, 4.74) * mm});
            skLineSegment(sketch, "E7.0.3.3", {"start": v(-110.55, 18.74) * mm, "end": v(-110.55, 4.74) * mm});
            skLineSegment(sketch, "E7.0.4.0", {"start": v(-110.55, -14.26) * mm, "end": v(-96.55, -14.26) * mm});
            skLineSegment(sketch, "E7.0.4.1", {"start": v(-96.55, -14.26) * mm, "end": v(-96.55, -28.26) * mm});
            skLineSegment(sketch, "E7.0.4.2", {"start": v(-110.55, -28.26) * mm, "end": v(-96.55, -28.26) * mm});
            skLineSegment(sketch, "E7.0.4.3", {"start": v(-110.55, -14.26) * mm, "end": v(-110.55, -28.26) * mm});
            skLineSegment(sketch, "E7.0.5.0", {"start": v(-110.55, -47.26) * mm, "end": v(-96.55, -47.26) * mm});
            skLineSegment(sketch, "E7.0.5.1", {"start": v(-96.55, -47.26) * mm, "end": v(-96.55, -61.26) * mm});
            skLineSegment(sketch, "E7.0.5.2", {"start": v(-110.55, -61.26) * mm, "end": v(-96.55, -61.26) * mm});
            skLineSegment(sketch, "E7.0.5.3", {"start": v(-110.55, -47.26) * mm, "end": v(-110.55, -61.26) * mm});
            skLineSegment(sketch, "E7.1.0.0", {"start": v(-94.05, 117.74) * mm, "end": v(-80.05, 117.74) * mm});
            skLineSegment(sketch, "E7.1.0.1", {"start": v(-80.05, 117.74) * mm, "end": v(-80.05, 103.74) * mm});
            skLineSegment(sketch, "E7.1.0.2", {"start": v(-94.05, 103.74) * mm, "end": v(-80.05, 103.74) * mm});
            skLineSegment(sketch, "E7.1.0.3", {"start": v(-94.05, 117.74) * mm, "end": v(-94.05, 103.74) * mm});
            skLineSegment(sketch, "E7.1.1.0", {"start": v(-94.05, 84.74) * mm, "end": v(-80.05, 84.74) * mm});
            skLineSegment(sketch, "E7.1.1.1", {"start": v(-80.05, 84.74) * mm, "end": v(-80.05, 70.74) * mm});
            skLineSegment(sketch, "E7.1.1.2", {"start": v(-94.05, 70.74) * mm, "end": v(-80.05, 70.74) * mm});
            skLineSegment(sketch, "E7.1.1.3", {"start": v(-94.05, 84.74) * mm, "end": v(-94.05, 70.74) * mm});
            skLineSegment(sketch, "E7.1.2.0", {"start": v(-94.05, 51.74) * mm, "end": v(-80.05, 51.74) * mm});
            skLineSegment(sketch, "E7.1.2.1", {"start": v(-80.05, 51.74) * mm, "end": v(-80.05, 37.74) * mm});
            skLineSegment(sketch, "E7.1.2.2", {"start": v(-94.05, 37.74) * mm, "end": v(-80.05, 37.74) * mm});
            skLineSegment(sketch, "E7.1.2.3", {"start": v(-94.05, 51.74) * mm, "end": v(-94.05, 37.74) * mm});
            skLineSegment(sketch, "E7.1.3.0", {"start": v(-94.05, 18.74) * mm, "end": v(-80.05, 18.74) * mm});
            skLineSegment(sketch, "E7.1.3.1", {"start": v(-80.05, 18.74) * mm, "end": v(-80.05, 4.74) * mm});
            skLineSegment(sketch, "E7.1.3.2", {"start": v(-94.05, 4.74) * mm, "end": v(-80.05, 4.74) * mm});
            skLineSegment(sketch, "E7.1.3.3", {"start": v(-94.05, 18.74) * mm, "end": v(-94.05, 4.74) * mm});
            skLineSegment(sketch, "E7.1.4.0", {"start": v(-94.05, -14.26) * mm, "end": v(-80.05, -14.26) * mm});
            skLineSegment(sketch, "E7.1.4.1", {"start": v(-80.05, -14.26) * mm, "end": v(-80.05, -28.26) * mm});
            skLineSegment(sketch, "E7.1.4.2", {"start": v(-94.05, -28.26) * mm, "end": v(-80.05, -28.26) * mm});
            skLineSegment(sketch, "E7.1.4.3", {"start": v(-94.05, -14.26) * mm, "end": v(-94.05, -28.26) * mm});
            skLineSegment(sketch, "E7.1.5.0", {"start": v(-94.05, -47.26) * mm, "end": v(-80.05, -47.26) * mm});
            skLineSegment(sketch, "E7.1.5.1", {"start": v(-80.05, -47.26) * mm, "end": v(-80.05, -61.26) * mm});
            skLineSegment(sketch, "E7.1.5.2", {"start": v(-94.05, -61.26) * mm, "end": v(-80.05, -61.26) * mm});
            skLineSegment(sketch, "E7.1.5.3", {"start": v(-94.05, -47.26) * mm, "end": v(-94.05, -61.26) * mm});
            skLineSegment(sketch, "E7.2.0.0", {"start": v(-77.55, 117.74) * mm, "end": v(-63.55, 117.74) * mm});
            skLineSegment(sketch, "E7.2.0.1", {"start": v(-63.55, 117.74) * mm, "end": v(-63.55, 103.74) * mm});
            skLineSegment(sketch, "E7.2.0.2", {"start": v(-77.55, 103.74) * mm, "end": v(-63.55, 103.74) * mm});
            skLineSegment(sketch, "E7.2.0.3", {"start": v(-77.55, 117.74) * mm, "end": v(-77.55, 103.74) * mm});
            skLineSegment(sketch, "E7.2.1.0", {"start": v(-77.55, 84.74) * mm, "end": v(-63.55, 84.74) * mm});
            skLineSegment(sketch, "E7.2.1.1", {"start": v(-63.55, 84.74) * mm, "end": v(-63.55, 70.74) * mm});
            skLineSegment(sketch, "E7.2.1.2", {"start": v(-77.55, 70.74) * mm, "end": v(-63.55, 70.74) * mm});
            skLineSegment(sketch, "E7.2.1.3", {"start": v(-77.55, 84.74) * mm, "end": v(-77.55, 70.74) * mm});
            skLineSegment(sketch, "E7.2.2.0", {"start": v(-77.55, 51.74) * mm, "end": v(-63.55, 51.74) * mm});
            skLineSegment(sketch, "E7.2.2.1", {"start": v(-63.55, 51.74) * mm, "end": v(-63.55, 37.74) * mm});
            skLineSegment(sketch, "E7.2.2.2", {"start": v(-77.55, 37.74) * mm, "end": v(-63.55, 37.74) * mm});
            skLineSegment(sketch, "E7.2.2.3", {"start": v(-77.55, 51.74) * mm, "end": v(-77.55, 37.74) * mm});
            skLineSegment(sketch, "E7.2.3.0", {"start": v(-77.55, 18.74) * mm, "end": v(-63.55, 18.74) * mm});
            skLineSegment(sketch, "E7.2.3.1", {"start": v(-63.55, 18.74) * mm, "end": v(-63.55, 4.74) * mm});
            skLineSegment(sketch, "E7.2.3.2", {"start": v(-77.55, 4.74) * mm, "end": v(-63.55, 4.74) * mm});
            skLineSegment(sketch, "E7.2.3.3", {"start": v(-77.55, 18.74) * mm, "end": v(-77.55, 4.74) * mm});
            skLineSegment(sketch, "E7.2.4.0", {"start": v(-77.55, -14.26) * mm, "end": v(-63.55, -14.26) * mm});
            skLineSegment(sketch, "E7.2.4.1", {"start": v(-63.55, -14.26) * mm, "end": v(-63.55, -28.26) * mm});
            skLineSegment(sketch, "E7.2.4.2", {"start": v(-77.55, -28.26) * mm, "end": v(-63.55, -28.26) * mm});
            skLineSegment(sketch, "E7.2.4.3", {"start": v(-77.55, -14.26) * mm, "end": v(-77.55, -28.26) * mm});
            skLineSegment(sketch, "E7.2.5.0", {"start": v(-77.55, -47.26) * mm, "end": v(-63.55, -47.26) * mm});
            skLineSegment(sketch, "E7.2.5.1", {"start": v(-63.55, -47.26) * mm, "end": v(-63.55, -61.26) * mm});
            skLineSegment(sketch, "E7.2.5.2", {"start": v(-77.55, -61.26) * mm, "end": v(-63.55, -61.26) * mm});
            skLineSegment(sketch, "E7.2.5.3", {"start": v(-77.55, -47.26) * mm, "end": v(-77.55, -61.26) * mm});
            skLineSegment(sketch, "E7.3.0.0", {"start": v(-61.05, 117.74) * mm, "end": v(-47.05, 117.74) * mm});
            skLineSegment(sketch, "E7.3.0.1", {"start": v(-47.05, 117.74) * mm, "end": v(-47.05, 103.74) * mm});
            skLineSegment(sketch, "E7.3.0.2", {"start": v(-61.05, 103.74) * mm, "end": v(-47.05, 103.74) * mm});
            skLineSegment(sketch, "E7.3.0.3", {"start": v(-61.05, 117.74) * mm, "end": v(-61.05, 103.74) * mm});
            skLineSegment(sketch, "E7.3.1.0", {"start": v(-61.05, 84.74) * mm, "end": v(-47.05, 84.74) * mm});
            skLineSegment(sketch, "E7.3.1.1", {"start": v(-47.05, 84.74) * mm, "end": v(-47.05, 70.74) * mm});
            skLineSegment(sketch, "E7.3.1.2", {"start": v(-61.05, 70.74) * mm, "end": v(-47.05, 70.74) * mm});
            skLineSegment(sketch, "E7.3.1.3", {"start": v(-61.05, 84.74) * mm, "end": v(-61.05, 70.74) * mm});
            skLineSegment(sketch, "E7.3.2.0", {"start": v(-61.05, 51.74) * mm, "end": v(-47.05, 51.74) * mm});
            skLineSegment(sketch, "E7.3.2.1", {"start": v(-47.05, 51.74) * mm, "end": v(-47.05, 37.74) * mm});
            skLineSegment(sketch, "E7.3.2.2", {"start": v(-61.05, 37.74) * mm, "end": v(-47.05, 37.74) * mm});
            skLineSegment(sketch, "E7.3.2.3", {"start": v(-61.05, 51.74) * mm, "end": v(-61.05, 37.74) * mm});
            skLineSegment(sketch, "E7.3.3.0", {"start": v(-61.05, 18.74) * mm, "end": v(-47.05, 18.74) * mm});
            skLineSegment(sketch, "E7.3.3.1", {"start": v(-47.05, 18.74) * mm, "end": v(-47.05, 4.74) * mm});
            skLineSegment(sketch, "E7.3.3.2", {"start": v(-61.05, 4.74) * mm, "end": v(-47.05, 4.74) * mm});
            skLineSegment(sketch, "E7.3.3.3", {"start": v(-61.05, 18.74) * mm, "end": v(-61.05, 4.74) * mm});
            skLineSegment(sketch, "E7.3.4.0", {"start": v(-61.05, -14.26) * mm, "end": v(-47.05, -14.26) * mm});
            skLineSegment(sketch, "E7.3.4.1", {"start": v(-47.05, -14.26) * mm, "end": v(-47.05, -28.26) * mm});
            skLineSegment(sketch, "E7.3.4.2", {"start": v(-61.05, -28.26) * mm, "end": v(-47.05, -28.26) * mm});
            skLineSegment(sketch, "E7.3.4.3", {"start": v(-61.05, -14.26) * mm, "end": v(-61.05, -28.26) * mm});
            skLineSegment(sketch, "E7.3.5.0", {"start": v(-61.05, -47.26) * mm, "end": v(-47.05, -47.26) * mm});
            skLineSegment(sketch, "E7.3.5.1", {"start": v(-47.05, -47.26) * mm, "end": v(-47.05, -61.26) * mm});
            skLineSegment(sketch, "E7.3.5.2", {"start": v(-61.05, -61.26) * mm, "end": v(-47.05, -61.26) * mm});
            skLineSegment(sketch, "E7.3.5.3", {"start": v(-61.05, -47.26) * mm, "end": v(-61.05, -61.26) * mm});
            skLineSegment(sketch, "E7.4.0.0", {"start": v(-44.55, 117.74) * mm, "end": v(-30.55, 117.74) * mm});
            skLineSegment(sketch, "E7.4.0.1", {"start": v(-30.55, 117.74) * mm, "end": v(-30.55, 103.74) * mm});
            skLineSegment(sketch, "E7.4.0.2", {"start": v(-44.55, 103.74) * mm, "end": v(-30.55, 103.74) * mm});
            skLineSegment(sketch, "E7.4.0.3", {"start": v(-44.55, 117.74) * mm, "end": v(-44.55, 103.74) * mm});
            skLineSegment(sketch, "E7.4.1.0", {"start": v(-44.55, 84.74) * mm, "end": v(-30.55, 84.74) * mm});
            skLineSegment(sketch, "E7.4.1.1", {"start": v(-30.55, 84.74) * mm, "end": v(-30.55, 70.74) * mm});
            skLineSegment(sketch, "E7.4.1.2", {"start": v(-44.55, 70.74) * mm, "end": v(-30.55, 70.74) * mm});
            skLineSegment(sketch, "E7.4.1.3", {"start": v(-44.55, 84.74) * mm, "end": v(-44.55, 70.74) * mm});
            skLineSegment(sketch, "E7.4.2.0", {"start": v(-44.55, 51.74) * mm, "end": v(-30.55, 51.74) * mm});
            skLineSegment(sketch, "E7.4.2.1", {"start": v(-30.55, 51.74) * mm, "end": v(-30.55, 37.74) * mm});
            skLineSegment(sketch, "E7.4.2.2", {"start": v(-44.55, 37.74) * mm, "end": v(-30.55, 37.74) * mm});
            skLineSegment(sketch, "E7.4.2.3", {"start": v(-44.55, 51.74) * mm, "end": v(-44.55, 37.74) * mm});
            skLineSegment(sketch, "E7.4.3.0", {"start": v(-44.55, 18.74) * mm, "end": v(-30.55, 18.74) * mm});
            skLineSegment(sketch, "E7.4.3.1", {"start": v(-30.55, 18.74) * mm, "end": v(-30.55, 4.74) * mm});
            skLineSegment(sketch, "E7.4.3.2", {"start": v(-44.55, 4.74) * mm, "end": v(-30.55, 4.74) * mm});
            skLineSegment(sketch, "E7.4.3.3", {"start": v(-44.55, 18.74) * mm, "end": v(-44.55, 4.74) * mm});
            skLineSegment(sketch, "E7.4.4.0", {"start": v(-44.55, -14.26) * mm, "end": v(-30.55, -14.26) * mm});
            skLineSegment(sketch, "E7.4.4.1", {"start": v(-30.55, -14.26) * mm, "end": v(-30.55, -28.26) * mm});
            skLineSegment(sketch, "E7.4.4.2", {"start": v(-44.55, -28.26) * mm, "end": v(-30.55, -28.26) * mm});
            skLineSegment(sketch, "E7.4.4.3", {"start": v(-44.55, -14.26) * mm, "end": v(-44.55, -28.26) * mm});
            skLineSegment(sketch, "E7.4.5.0", {"start": v(-44.55, -47.26) * mm, "end": v(-30.55, -47.26) * mm});
            skLineSegment(sketch, "E7.4.5.1", {"start": v(-30.55, -47.26) * mm, "end": v(-30.55, -61.26) * mm});
            skLineSegment(sketch, "E7.4.5.2", {"start": v(-44.55, -61.26) * mm, "end": v(-30.55, -61.26) * mm});
            skLineSegment(sketch, "E7.4.5.3", {"start": v(-44.55, -47.26) * mm, "end": v(-44.55, -61.26) * mm});
            skLineSegment(sketch, "E7.5.0.0", {"start": v(-28.05, 117.74) * mm, "end": v(-14.05, 117.74) * mm});
            skLineSegment(sketch, "E7.5.0.1", {"start": v(-14.05, 117.74) * mm, "end": v(-14.05, 103.74) * mm});
            skLineSegment(sketch, "E7.5.0.2", {"start": v(-28.05, 103.74) * mm, "end": v(-14.05, 103.74) * mm});
            skLineSegment(sketch, "E7.5.0.3", {"start": v(-28.05, 117.74) * mm, "end": v(-28.05, 103.74) * mm});
            skLineSegment(sketch, "E7.5.1.0", {"start": v(-28.05, 84.74) * mm, "end": v(-14.05, 84.74) * mm});
            skLineSegment(sketch, "E7.5.1.1", {"start": v(-14.05, 84.74) * mm, "end": v(-14.05, 70.74) * mm});
            skLineSegment(sketch, "E7.5.1.2", {"start": v(-28.05, 70.74) * mm, "end": v(-14.05, 70.74) * mm});
            skLineSegment(sketch, "E7.5.1.3", {"start": v(-28.05, 84.74) * mm, "end": v(-28.05, 70.74) * mm});
            skLineSegment(sketch, "E7.5.2.0", {"start": v(-28.05, 51.74) * mm, "end": v(-14.05, 51.74) * mm});
            skLineSegment(sketch, "E7.5.2.1", {"start": v(-14.05, 51.74) * mm, "end": v(-14.05, 37.74) * mm});
            skLineSegment(sketch, "E7.5.2.2", {"start": v(-28.05, 37.74) * mm, "end": v(-14.05, 37.74) * mm});
            skLineSegment(sketch, "E7.5.2.3", {"start": v(-28.05, 51.74) * mm, "end": v(-28.05, 37.74) * mm});
            skLineSegment(sketch, "E7.5.3.0", {"start": v(-28.05, 18.74) * mm, "end": v(-14.05, 18.74) * mm});
            skLineSegment(sketch, "E7.5.3.1", {"start": v(-14.05, 18.74) * mm, "end": v(-14.05, 4.74) * mm});
            skLineSegment(sketch, "E7.5.3.2", {"start": v(-28.05, 4.74) * mm, "end": v(-14.05, 4.74) * mm});
            skLineSegment(sketch, "E7.5.3.3", {"start": v(-28.05, 18.74) * mm, "end": v(-28.05, 4.74) * mm});
            skLineSegment(sketch, "E7.5.4.0", {"start": v(-28.05, -14.26) * mm, "end": v(-14.05, -14.26) * mm});
            skLineSegment(sketch, "E7.5.4.1", {"start": v(-14.05, -14.26) * mm, "end": v(-14.05, -28.26) * mm});
            skLineSegment(sketch, "E7.5.4.2", {"start": v(-28.05, -28.26) * mm, "end": v(-14.05, -28.26) * mm});
            skLineSegment(sketch, "E7.5.4.3", {"start": v(-28.05, -14.26) * mm, "end": v(-28.05, -28.26) * mm});
            skLineSegment(sketch, "E7.5.5.0", {"start": v(-28.05, -47.26) * mm, "end": v(-14.05, -47.26) * mm});
            skLineSegment(sketch, "E7.5.5.1", {"start": v(-14.05, -47.26) * mm, "end": v(-14.05, -61.26) * mm});
            skLineSegment(sketch, "E7.5.5.2", {"start": v(-28.05, -61.26) * mm, "end": v(-14.05, -61.26) * mm});
            skLineSegment(sketch, "E7.5.5.3", {"start": v(-28.05, -47.26) * mm, "end": v(-28.05, -61.26) * mm});
            skLineSegment(sketch, "E7.6.0.0", {"start": v(-11.55, 117.74) * mm, "end": v(2.45, 117.74) * mm});
            skLineSegment(sketch, "E7.6.0.1", {"start": v(2.45, 117.74) * mm, "end": v(2.45, 103.74) * mm});
            skLineSegment(sketch, "E7.6.0.2", {"start": v(-11.55, 103.74) * mm, "end": v(2.45, 103.74) * mm});
            skLineSegment(sketch, "E7.6.0.3", {"start": v(-11.55, 117.74) * mm, "end": v(-11.55, 103.74) * mm});
            skLineSegment(sketch, "E7.6.1.0", {"start": v(-11.55, 84.74) * mm, "end": v(2.45, 84.74) * mm});
            skLineSegment(sketch, "E7.6.1.1", {"start": v(2.45, 84.74) * mm, "end": v(2.45, 70.74) * mm});
            skLineSegment(sketch, "E7.6.1.2", {"start": v(-11.55, 70.74) * mm, "end": v(2.45, 70.74) * mm});
            skLineSegment(sketch, "E7.6.1.3", {"start": v(-11.55, 84.74) * mm, "end": v(-11.55, 70.74) * mm});
            skLineSegment(sketch, "E7.6.2.0", {"start": v(-11.55, 51.74) * mm, "end": v(2.45, 51.74) * mm});
            skLineSegment(sketch, "E7.6.2.1", {"start": v(2.45, 51.74) * mm, "end": v(2.45, 37.74) * mm});
            skLineSegment(sketch, "E7.6.2.2", {"start": v(-11.55, 37.74) * mm, "end": v(2.45, 37.74) * mm});
            skLineSegment(sketch, "E7.6.2.3", {"start": v(-11.55, 51.74) * mm, "end": v(-11.55, 37.74) * mm});
            skLineSegment(sketch, "E7.6.3.0", {"start": v(-11.55, 18.74) * mm, "end": v(2.45, 18.74) * mm});
            skLineSegment(sketch, "E7.6.3.1", {"start": v(2.45, 18.74) * mm, "end": v(2.45, 4.74) * mm});
            skLineSegment(sketch, "E7.6.3.2", {"start": v(-11.55, 4.74) * mm, "end": v(2.45, 4.74) * mm});
            skLineSegment(sketch, "E7.6.3.3", {"start": v(-11.55, 18.74) * mm, "end": v(-11.55, 4.74) * mm});
            skLineSegment(sketch, "E7.6.4.0", {"start": v(-11.55, -14.26) * mm, "end": v(2.45, -14.26) * mm});
            skLineSegment(sketch, "E7.6.4.1", {"start": v(2.45, -14.26) * mm, "end": v(2.45, -28.26) * mm});
            skLineSegment(sketch, "E7.6.4.2", {"start": v(-11.55, -28.26) * mm, "end": v(2.45, -28.26) * mm});
            skLineSegment(sketch, "E7.6.4.3", {"start": v(-11.55, -14.26) * mm, "end": v(-11.55, -28.26) * mm});
            skLineSegment(sketch, "E7.6.5.0", {"start": v(-11.55, -47.26) * mm, "end": v(2.45, -47.26) * mm});
            skLineSegment(sketch, "E7.6.5.1", {"start": v(2.45, -47.26) * mm, "end": v(2.45, -61.26) * mm});
            skLineSegment(sketch, "E7.6.5.2", {"start": v(-11.55, -61.26) * mm, "end": v(2.45, -61.26) * mm});
            skLineSegment(sketch, "E7.6.5.3", {"start": v(-11.55, -47.26) * mm, "end": v(-11.55, -61.26) * mm});
            skLineSegment(sketch, "E7.7.0.0", {"start": v(4.95, 117.74) * mm, "end": v(18.95, 117.74) * mm});
            skLineSegment(sketch, "E7.7.0.1", {"start": v(18.95, 117.74) * mm, "end": v(18.95, 103.74) * mm});
            skLineSegment(sketch, "E7.7.0.2", {"start": v(4.95, 103.74) * mm, "end": v(18.95, 103.74) * mm});
            skLineSegment(sketch, "E7.7.0.3", {"start": v(4.95, 117.74) * mm, "end": v(4.95, 103.74) * mm});
            skLineSegment(sketch, "E7.7.1.0", {"start": v(4.95, 84.74) * mm, "end": v(18.95, 84.74) * mm});
            skLineSegment(sketch, "E7.7.1.1", {"start": v(18.95, 84.74) * mm, "end": v(18.95, 70.74) * mm});
            skLineSegment(sketch, "E7.7.1.2", {"start": v(4.95, 70.74) * mm, "end": v(18.95, 70.74) * mm});
            skLineSegment(sketch, "E7.7.1.3", {"start": v(4.95, 84.74) * mm, "end": v(4.95, 70.74) * mm});
            skLineSegment(sketch, "E7.7.2.0", {"start": v(4.95, 51.74) * mm, "end": v(18.95, 51.74) * mm});
            skLineSegment(sketch, "E7.7.2.1", {"start": v(18.95, 51.74) * mm, "end": v(18.95, 37.74) * mm});
            skLineSegment(sketch, "E7.7.2.2", {"start": v(4.95, 37.74) * mm, "end": v(18.95, 37.74) * mm});
            skLineSegment(sketch, "E7.7.2.3", {"start": v(4.95, 51.74) * mm, "end": v(4.95, 37.74) * mm});
            skLineSegment(sketch, "E7.7.3.0", {"start": v(4.95, 18.74) * mm, "end": v(18.95, 18.74) * mm});
            skLineSegment(sketch, "E7.7.3.1", {"start": v(18.95, 18.74) * mm, "end": v(18.95, 4.74) * mm});
            skLineSegment(sketch, "E7.7.3.2", {"start": v(4.95, 4.74) * mm, "end": v(18.95, 4.74) * mm});
            skLineSegment(sketch, "E7.7.3.3", {"start": v(4.95, 18.74) * mm, "end": v(4.95, 4.74) * mm});
            skLineSegment(sketch, "E7.7.4.0", {"start": v(4.95, -14.26) * mm, "end": v(18.95, -14.26) * mm});
            skLineSegment(sketch, "E7.7.4.1", {"start": v(18.95, -14.26) * mm, "end": v(18.95, -28.26) * mm});
            skLineSegment(sketch, "E7.7.4.2", {"start": v(4.95, -28.26) * mm, "end": v(18.95, -28.26) * mm});
            skLineSegment(sketch, "E7.7.4.3", {"start": v(4.95, -14.26) * mm, "end": v(4.95, -28.26) * mm});
            skLineSegment(sketch, "E7.7.5.0", {"start": v(4.95, -47.26) * mm, "end": v(18.95, -47.26) * mm});
            skLineSegment(sketch, "E7.7.5.1", {"start": v(18.95, -47.26) * mm, "end": v(18.95, -61.26) * mm});
            skLineSegment(sketch, "E7.7.5.2", {"start": v(4.95, -61.26) * mm, "end": v(18.95, -61.26) * mm});
            skLineSegment(sketch, "E7.7.5.3", {"start": v(4.95, -47.26) * mm, "end": v(4.95, -61.26) * mm});
            skLineSegment(sketch, "E7.8.0.0", {"start": v(21.45, 117.74) * mm, "end": v(35.45, 117.74) * mm});
            skLineSegment(sketch, "E7.8.0.1", {"start": v(35.45, 117.74) * mm, "end": v(35.45, 103.74) * mm});
            skLineSegment(sketch, "E7.8.0.2", {"start": v(21.45, 103.74) * mm, "end": v(35.45, 103.74) * mm});
            skLineSegment(sketch, "E7.8.0.3", {"start": v(21.45, 117.74) * mm, "end": v(21.45, 103.74) * mm});
            skLineSegment(sketch, "E7.8.1.0", {"start": v(21.45, 84.74) * mm, "end": v(35.45, 84.74) * mm});
            skLineSegment(sketch, "E7.8.1.1", {"start": v(35.45, 84.74) * mm, "end": v(35.45, 70.74) * mm});
            skLineSegment(sketch, "E7.8.1.2", {"start": v(21.45, 70.74) * mm, "end": v(35.45, 70.74) * mm});
            skLineSegment(sketch, "E7.8.1.3", {"start": v(21.45, 84.74) * mm, "end": v(21.45, 70.74) * mm});
            skLineSegment(sketch, "E7.8.2.0", {"start": v(21.45, 51.74) * mm, "end": v(35.45, 51.74) * mm});
            skLineSegment(sketch, "E7.8.2.1", {"start": v(35.45, 51.74) * mm, "end": v(35.45, 37.74) * mm});
            skLineSegment(sketch, "E7.8.2.2", {"start": v(21.45, 37.74) * mm, "end": v(35.45, 37.74) * mm});
            skLineSegment(sketch, "E7.8.2.3", {"start": v(21.45, 51.74) * mm, "end": v(21.45, 37.74) * mm});
            skLineSegment(sketch, "E7.8.3.0", {"start": v(21.45, 18.74) * mm, "end": v(35.45, 18.74) * mm});
            skLineSegment(sketch, "E7.8.3.1", {"start": v(35.45, 18.74) * mm, "end": v(35.45, 4.74) * mm});
            skLineSegment(sketch, "E7.8.3.2", {"start": v(21.45, 4.74) * mm, "end": v(35.45, 4.74) * mm});
            skLineSegment(sketch, "E7.8.3.3", {"start": v(21.45, 18.74) * mm, "end": v(21.45, 4.74) * mm});
            skLineSegment(sketch, "E7.8.4.0", {"start": v(21.45, -14.26) * mm, "end": v(35.45, -14.26) * mm});
            skLineSegment(sketch, "E7.8.4.1", {"start": v(35.45, -14.26) * mm, "end": v(35.45, -28.26) * mm});
            skLineSegment(sketch, "E7.8.4.2", {"start": v(21.45, -28.26) * mm, "end": v(35.45, -28.26) * mm});
            skLineSegment(sketch, "E7.8.4.3", {"start": v(21.45, -14.26) * mm, "end": v(21.45, -28.26) * mm});
            skLineSegment(sketch, "E7.8.5.0", {"start": v(21.45, -47.26) * mm, "end": v(35.45, -47.26) * mm});
            skLineSegment(sketch, "E7.8.5.1", {"start": v(35.45, -47.26) * mm, "end": v(35.45, -61.26) * mm});
            skLineSegment(sketch, "E7.8.5.2", {"start": v(21.45, -61.26) * mm, "end": v(35.45, -61.26) * mm});
            skLineSegment(sketch, "E7.8.5.3", {"start": v(21.45, -47.26) * mm, "end": v(21.45, -61.26) * mm});
            skLineSegment(sketch, "E7.9.0.0", {"start": v(37.95, 117.74) * mm, "end": v(51.95, 117.74) * mm});
            skLineSegment(sketch, "E7.9.0.1", {"start": v(51.95, 117.74) * mm, "end": v(51.95, 103.74) * mm});
            skLineSegment(sketch, "E7.9.0.2", {"start": v(37.95, 103.74) * mm, "end": v(51.95, 103.74) * mm});
            skLineSegment(sketch, "E7.9.0.3", {"start": v(37.95, 117.74) * mm, "end": v(37.95, 103.74) * mm});
            skLineSegment(sketch, "E7.9.1.0", {"start": v(37.95, 84.74) * mm, "end": v(51.95, 84.74) * mm});
            skLineSegment(sketch, "E7.9.1.1", {"start": v(51.95, 84.74) * mm, "end": v(51.95, 70.74) * mm});
            skLineSegment(sketch, "E7.9.1.2", {"start": v(37.95, 70.74) * mm, "end": v(51.95, 70.74) * mm});
            skLineSegment(sketch, "E7.9.1.3", {"start": v(37.95, 84.74) * mm, "end": v(37.95, 70.74) * mm});
            skLineSegment(sketch, "E7.9.2.0", {"start": v(37.95, 51.74) * mm, "end": v(51.95, 51.74) * mm});
            skLineSegment(sketch, "E7.9.2.1", {"start": v(51.95, 51.74) * mm, "end": v(51.95, 37.74) * mm});
            skLineSegment(sketch, "E7.9.2.2", {"start": v(37.95, 37.74) * mm, "end": v(51.95, 37.74) * mm});
            skLineSegment(sketch, "E7.9.2.3", {"start": v(37.95, 51.74) * mm, "end": v(37.95, 37.74) * mm});
            skLineSegment(sketch, "E7.9.3.0", {"start": v(37.95, 18.74) * mm, "end": v(51.95, 18.74) * mm});
            skLineSegment(sketch, "E7.9.3.1", {"start": v(51.95, 18.74) * mm, "end": v(51.95, 4.74) * mm});
            skLineSegment(sketch, "E7.9.3.2", {"start": v(37.95, 4.74) * mm, "end": v(51.95, 4.74) * mm});
            skLineSegment(sketch, "E7.9.3.3", {"start": v(37.95, 18.74) * mm, "end": v(37.95, 4.74) * mm});
            skLineSegment(sketch, "E7.9.4.0", {"start": v(37.95, -14.26) * mm, "end": v(51.95, -14.26) * mm});
            skLineSegment(sketch, "E7.9.4.1", {"start": v(51.95, -14.26) * mm, "end": v(51.95, -28.26) * mm});
            skLineSegment(sketch, "E7.9.4.2", {"start": v(37.95, -28.26) * mm, "end": v(51.95, -28.26) * mm});
            skLineSegment(sketch, "E7.9.4.3", {"start": v(37.95, -14.26) * mm, "end": v(37.95, -28.26) * mm});
            skLineSegment(sketch, "E7.9.5.0", {"start": v(37.95, -47.26) * mm, "end": v(51.95, -47.26) * mm});
            skLineSegment(sketch, "E7.9.5.1", {"start": v(51.95, -47.26) * mm, "end": v(51.95, -61.26) * mm});
            skLineSegment(sketch, "E7.9.5.2", {"start": v(37.95, -61.26) * mm, "end": v(51.95, -61.26) * mm});
            skLineSegment(sketch, "E7.9.5.3", {"start": v(37.95, -47.26) * mm, "end": v(37.95, -61.26) * mm});
            skLineSegment(sketch, "E7.10.0.0", {"start": v(54.45, 117.74) * mm, "end": v(68.45, 117.74) * mm});
            skLineSegment(sketch, "E7.10.0.1", {"start": v(68.45, 117.74) * mm, "end": v(68.45, 103.74) * mm});
            skLineSegment(sketch, "E7.10.0.2", {"start": v(54.45, 103.74) * mm, "end": v(68.45, 103.74) * mm});
            skLineSegment(sketch, "E7.10.0.3", {"start": v(54.45, 117.74) * mm, "end": v(54.45, 103.74) * mm});
            skLineSegment(sketch, "E7.10.1.0", {"start": v(54.45, 84.74) * mm, "end": v(68.45, 84.74) * mm});
            skLineSegment(sketch, "E7.10.1.1", {"start": v(68.45, 84.74) * mm, "end": v(68.45, 70.74) * mm});
            skLineSegment(sketch, "E7.10.1.2", {"start": v(54.45, 70.74) * mm, "end": v(68.45, 70.74) * mm});
            skLineSegment(sketch, "E7.10.1.3", {"start": v(54.45, 84.74) * mm, "end": v(54.45, 70.74) * mm});
            skLineSegment(sketch, "E7.10.2.0", {"start": v(54.45, 51.74) * mm, "end": v(68.45, 51.74) * mm});
            skLineSegment(sketch, "E7.10.2.1", {"start": v(68.45, 51.74) * mm, "end": v(68.45, 37.74) * mm});
            skLineSegment(sketch, "E7.10.2.2", {"start": v(54.45, 37.74) * mm, "end": v(68.45, 37.74) * mm});
            skLineSegment(sketch, "E7.10.2.3", {"start": v(54.45, 51.74) * mm, "end": v(54.45, 37.74) * mm});
            skLineSegment(sketch, "E7.10.3.0", {"start": v(54.45, 18.74) * mm, "end": v(68.45, 18.74) * mm});
            skLineSegment(sketch, "E7.10.3.1", {"start": v(68.45, 18.74) * mm, "end": v(68.45, 4.74) * mm});
            skLineSegment(sketch, "E7.10.3.2", {"start": v(54.45, 4.74) * mm, "end": v(68.45, 4.74) * mm});
            skLineSegment(sketch, "E7.10.3.3", {"start": v(54.45, 18.74) * mm, "end": v(54.45, 4.74) * mm});
            skLineSegment(sketch, "E7.10.4.0", {"start": v(54.45, -14.26) * mm, "end": v(68.45, -14.26) * mm});
            skLineSegment(sketch, "E7.10.4.1", {"start": v(68.45, -14.26) * mm, "end": v(68.45, -28.26) * mm});
            skLineSegment(sketch, "E7.10.4.2", {"start": v(54.45, -28.26) * mm, "end": v(68.45, -28.26) * mm});
            skLineSegment(sketch, "E7.10.4.3", {"start": v(54.45, -14.26) * mm, "end": v(54.45, -28.26) * mm});
            skLineSegment(sketch, "E7.10.5.0", {"start": v(54.45, -47.26) * mm, "end": v(68.45, -47.26) * mm});
            skLineSegment(sketch, "E7.10.5.1", {"start": v(68.45, -47.26) * mm, "end": v(68.45, -61.26) * mm});
            skLineSegment(sketch, "E7.10.5.2", {"start": v(54.45, -61.26) * mm, "end": v(68.45, -61.26) * mm});
            skLineSegment(sketch, "E7.10.5.3", {"start": v(54.45, -47.26) * mm, "end": v(54.45, -61.26) * mm});
            skLineSegment(sketch, "E7.11.0.0", {"start": v(70.95, 117.74) * mm, "end": v(84.95, 117.74) * mm});
            skLineSegment(sketch, "E7.11.0.1", {"start": v(84.95, 117.74) * mm, "end": v(84.95, 103.74) * mm});
            skLineSegment(sketch, "E7.11.0.2", {"start": v(70.95, 103.74) * mm, "end": v(84.95, 103.74) * mm});
            skLineSegment(sketch, "E7.11.0.3", {"start": v(70.95, 117.74) * mm, "end": v(70.95, 103.74) * mm});
            skLineSegment(sketch, "E7.11.1.0", {"start": v(70.95, 84.74) * mm, "end": v(84.95, 84.74) * mm});
            skLineSegment(sketch, "E7.11.1.1", {"start": v(84.95, 84.74) * mm, "end": v(84.95, 70.74) * mm});
            skLineSegment(sketch, "E7.11.1.2", {"start": v(70.95, 70.74) * mm, "end": v(84.95, 70.74) * mm});
            skLineSegment(sketch, "E7.11.1.3", {"start": v(70.95, 84.74) * mm, "end": v(70.95, 70.74) * mm});
            skLineSegment(sketch, "E7.11.2.0", {"start": v(70.95, 51.74) * mm, "end": v(84.95, 51.74) * mm});
            skLineSegment(sketch, "E7.11.2.1", {"start": v(84.95, 51.74) * mm, "end": v(84.95, 37.74) * mm});
            skLineSegment(sketch, "E7.11.2.2", {"start": v(70.95, 37.74) * mm, "end": v(84.95, 37.74) * mm});
            skLineSegment(sketch, "E7.11.2.3", {"start": v(70.95, 51.74) * mm, "end": v(70.95, 37.74) * mm});
            skLineSegment(sketch, "E7.11.3.0", {"start": v(70.95, 18.74) * mm, "end": v(84.95, 18.74) * mm});
            skLineSegment(sketch, "E7.11.3.1", {"start": v(84.95, 18.74) * mm, "end": v(84.95, 4.74) * mm});
            skLineSegment(sketch, "E7.11.3.2", {"start": v(70.95, 4.74) * mm, "end": v(84.95, 4.74) * mm});
            skLineSegment(sketch, "E7.11.3.3", {"start": v(70.95, 18.74) * mm, "end": v(70.95, 4.74) * mm});
            skLineSegment(sketch, "E7.11.4.0", {"start": v(70.95, -14.26) * mm, "end": v(84.95, -14.26) * mm});
            skLineSegment(sketch, "E7.11.4.1", {"start": v(84.95, -14.26) * mm, "end": v(84.95, -28.26) * mm});
            skLineSegment(sketch, "E7.11.4.2", {"start": v(70.95, -28.26) * mm, "end": v(84.95, -28.26) * mm});
            skLineSegment(sketch, "E7.11.4.3", {"start": v(70.95, -14.26) * mm, "end": v(70.95, -28.26) * mm});
            skLineSegment(sketch, "E7.11.5.0", {"start": v(70.95, -47.26) * mm, "end": v(84.95, -47.26) * mm});
            skLineSegment(sketch, "E7.11.5.1", {"start": v(84.95, -47.26) * mm, "end": v(84.95, -61.26) * mm});
            skLineSegment(sketch, "E7.11.5.2", {"start": v(70.95, -61.26) * mm, "end": v(84.95, -61.26) * mm});
            skLineSegment(sketch, "E7.11.5.3", {"start": v(70.95, -47.26) * mm, "end": v(70.95, -61.26) * mm});
            skLineSegment(sketch, "E7.direction1", {"start": v(-110.55, 117.74) * mm, "end": v(-94.05, 117.74) * mm, "construction": true});
            skLineSegment(sketch, "E7.direction2", {"start": v(-110.55, 117.74) * mm, "end": v(-110.55, 84.74) * mm, "construction": true});
            skSolve(sketch);
        }
        {
            var Q0;
            Q0=makeQuery(id+"F0.imprint","IMPRINT",FACE,{"disambiguationData":[TD([[makeQuery(id+"F0.imprint","IMPRINT",EDGE,{"derivedFrom":sQuery(id+"F0.wireOp",EDGE,"E0.bottom")}),-1.0]])]});
            extrude(context, id + "F1", {"entities" : qUnion([Q0]), "depth" : 3 * mm});
        }
        {
            var Q0;
            Q0=makeQuery(id+"F1.opExtrude","CAP_FACE",FACE,{"disambiguationData":[OSD([sQuery(id+"F0.wireOp",EDGE,"E0.bottom"),sQuery(id+"F0.wireOp",EDGE,"E0.top"),sQuery(id+"F0.wireOp",EDGE,"E0.left"),sQuery(id+"F0.wireOp",EDGE,"E0.right"),sQuery(id+"F0.wireOp",EDGE,"E1.bottom"),sQuery(id+"F0.wireOp",EDGE,"E1.top"),sQuery(id+"F0.wireOp",EDGE,"E1.left"),sQuery(id+"F0.wireOp",EDGE,"E1.right"),sQuery(id+"F0.wireOp",EDGE,"E4.3.1.0"),sQuery(id+"F0.wireOp",EDGE,"E4.6.1.0"),sQuery(id+"F0.wireOp",EDGE,"E4.9.1.0"),sQuery(id+"F0.wireOp",EDGE,"E4.12.1.0"),sQuery(id+"F0.wireOp",EDGE,"E4.3.2.0"),sQuery(id+"F0.wireOp",EDGE,"E4.6.2.0"),sQuery(id+"F0.wireOp",EDGE,"E4.9.2.0"),sQuery(id+"F0.wireOp",EDGE,"E4.12.2.0"),sQuery(id+"F0.wireOp",EDGE,"E4.3.3.0"),sQuery(id+"F0.wireOp",EDGE,"E4.6.3.0"),sQuery(id+"F0.wireOp",EDGE,"E4.9.3.0"),sQuery(id+"F0.wireOp",EDGE,"E4.12.3.0"),sQuery(id+"F0.wireOp",EDGE,"E4.3.4.0"),sQuery(id+"F0.wireOp",EDGE,"E4.6.4.0"),sQuery(id+"F0.wireOp",EDGE,"E4.9.4.0"),sQuery(id+"F0.wireOp",EDGE,"E4.12.4.0"),sQuery(id+"F0.wireOp",EDGE,"E4.3.5.0"),sQuery(id+"F0.wireOp",EDGE,"E4.6.5.0"),sQuery(id+"F0.wireOp",EDGE,"E4.9.5.0"),sQuery(id+"F0.wireOp",EDGE,"E4.12.5.0"),sQuery(id+"F0.wireOp",EDGE,"E4.3.6.0"),sQuery(id+"F0.wireOp",EDGE,"E4.6.6.0"),sQuery(id+"F0.wireOp",EDGE,"E4.9.6.0"),sQuery(id+"F0.wireOp",EDGE,"E4.12.6.0"),sQuery(id+"F0.wireOp",EDGE,"E4.3.7.0"),sQuery(id+"F0.wireOp",EDGE,"E4.6.7.0"),sQuery(id+"F0.wireOp",EDGE,"E4.9.7.0"),sQuery(id+"F0.wireOp",EDGE,"E4.12.7.0"),sQuery(id+"F0.wireOp",EDGE,"E4.3.8.0"),sQuery(id+"F0.wireOp",EDGE,"E4.6.8.0"),sQuery(id+"F0.wireOp",EDGE,"E4.9.8.0"),sQuery(id+"F0.wireOp",EDGE,"E4.12.8.0"),sQuery(id+"F0.wireOp",EDGE,"E4.3.9.0"),sQuery(id+"F0.wireOp",EDGE,"E4.6.9.0"),sQuery(id+"F0.wireOp",EDGE,"E4.9.9.0"),sQuery(id+"F0.wireOp",EDGE,"E4.12.9.0"),sQuery(id+"F0.wireOp",EDGE,"E4.3.10.0"),sQuery(id+"F0.wireOp",EDGE,"E4.6.10.0"),sQuery(id+"F0.wireOp",EDGE,"E4.9.10.0"),sQuery(id+"F0.wireOp",EDGE,"E4.12.10.0"),sQuery(id+"F0.wireOp",EDGE,"E4.3.11.0"),sQuery(id+"F0.wireOp",EDGE,"E4.6.11.0"),sQuery(id+"F0.wireOp",EDGE,"E4.9.11.0"),sQuery(id+"F0.wireOp",EDGE,"E4.12.11.0"),sQuery(id+"F0.wireOp",EDGE,"E5.3.0.1"),sQuery(id+"F0.wireOp",EDGE,"E5.6.0.1"),sQuery(id+"F0.wireOp",EDGE,"E5.9.0.1"),sQuery(id+"F0.wireOp",EDGE,"E5.12.0.1"),sQuery(id+"F0.wireOp",EDGE,"E5.3.0.2"),sQuery(id+"F0.wireOp",EDGE,"E5.6.0.2"),sQuery(id+"F0.wireOp",EDGE,"E5.9.0.2"),sQuery(id+"F0.wireOp",EDGE,"E5.12.0.2"),sQuery(id+"F0.wireOp",EDGE,"E5.3.0.3"),sQuery(id+"F0.wireOp",EDGE,"E5.6.0.3"),sQuery(id+"F0.wireOp",EDGE,"E5.9.0.3"),sQuery(id+"F0.wireOp",EDGE,"E5.12.0.3"),sQuery(id+"F0.wireOp",EDGE,"E5.3.0.4"),sQuery(id+"F0.wireOp",EDGE,"E5.6.0.4"),sQuery(id+"F0.wireOp",EDGE,"E5.9.0.4"),sQuery(id+"F0.wireOp",EDGE,"E5.12.0.4"),sQuery(id+"F0.wireOp",EDGE,"E5.3.0.5"),sQuery(id+"F0.wireOp",EDGE,"E5.6.0.5"),sQuery(id+"F0.wireOp",EDGE,"E5.9.0.5"),sQuery(id+"F0.wireOp",EDGE,"E5.12.0.5"),sQuery(id+"F0.wireOp",EDGE,"E5.3.1.1"),sQuery(id+"F0.wireOp",EDGE,"E5.6.1.1"),sQuery(id+"F0.wireOp",EDGE,"E5.9.1.1"),sQuery(id+"F0.wireOp",EDGE,"E5.12.1.1"),sQuery(id+"F0.wireOp",EDGE,"E5.3.1.2"),sQuery(id+"F0.wireOp",EDGE,"E5.6.1.2"),sQuery(id+"F0.wireOp",EDGE,"E5.9.1.2"),sQuery(id+"F0.wireOp",EDGE,"E5.12.1.2"),sQuery(id+"F0.wireOp",EDGE,"E5.3.1.3"),sQuery(id+"F0.wireOp",EDGE,"E5.6.1.3"),sQuery(id+"F0.wireOp",EDGE,"E5.9.1.3"),sQuery(id+"F0.wireOp",EDGE,"E5.12.1.3"),sQuery(id+"F0.wireOp",EDGE,"E5.3.1.4"),sQuery(id+"F0.wireOp",EDGE,"E5.6.1.4"),sQuery(id+"F0.wireOp",EDGE,"E5.9.1.4"),sQuery(id+"F0.wireOp",EDGE,"E5.12.1.4"),sQuery(id+"F0.wireOp",EDGE,"E5.3.1.5"),sQuery(id+"F0.wireOp",EDGE,"E5.6.1.5"),sQuery(id+"F0.wireOp",EDGE,"E5.9.1.5"),sQuery(id+"F0.wireOp",EDGE,"E5.12.1.5"),sQuery(id+"F0.wireOp",EDGE,"E5.3.2.1"),sQuery(id+"F0.wireOp",EDGE,"E5.6.2.1"),sQuery(id+"F0.wireOp",EDGE,"E5.9.2.1"),sQuery(id+"F0.wireOp",EDGE,"E5.12.2.1"),sQuery(id+"F0.wireOp",EDGE,"E5.3.2.2"),sQuery(id+"F0.wireOp",EDGE,"E5.6.2.2"),sQuery(id+"F0.wireOp",EDGE,"E5.9.2.2"),sQuery(id+"F0.wireOp",EDGE,"E5.12.2.2"),sQuery(id+"F0.wireOp",EDGE,"E5.3.2.3"),sQuery(id+"F0.wireOp",EDGE,"E5.6.2.3"),sQuery(id+"F0.wireOp",EDGE,"E5.9.2.3"),sQuery(id+"F0.wireOp",EDGE,"E5.12.2.3"),sQuery(id+"F0.wireOp",EDGE,"E5.3.2.4"),sQuery(id+"F0.wireOp",EDGE,"E5.6.2.4"),sQuery(id+"F0.wireOp",EDGE,"E5.9.2.4"),sQuery(id+"F0.wireOp",EDGE,"E5.12.2.4"),sQuery(id+"F0.wireOp",EDGE,"E5.3.2.5"),sQuery(id+"F0.wireOp",EDGE,"E5.6.2.5"),sQuery(id+"F0.wireOp",EDGE,"E5.9.2.5"),sQuery(id+"F0.wireOp",EDGE,"E5.12.2.5"),sQuery(id+"F0.wireOp",EDGE,"E5.3.3.1"),sQuery(id+"F0.wireOp",EDGE,"E5.6.3.1"),sQuery(id+"F0.wireOp",EDGE,"E5.9.3.1"),sQuery(id+"F0.wireOp",EDGE,"E5.12.3.1"),sQuery(id+"F0.wireOp",EDGE,"E5.3.3.2"),sQuery(id+"F0.wireOp",EDGE,"E5.6.3.2"),sQuery(id+"F0.wireOp",EDGE,"E5.9.3.2"),sQuery(id+"F0.wireOp",EDGE,"E5.12.3.2"),sQuery(id+"F0.wireOp",EDGE,"E5.3.3.3"),sQuery(id+"F0.wireOp",EDGE,"E5.6.3.3"),sQuery(id+"F0.wireOp",EDGE,"E5.9.3.3"),sQuery(id+"F0.wireOp",EDGE,"E5.12.3.3"),sQuery(id+"F0.wireOp",EDGE,"E5.3.3.4"),sQuery(id+"F0.wireOp",EDGE,"E5.6.3.4"),sQuery(id+"F0.wireOp",EDGE,"E5.9.3.4"),sQuery(id+"F0.wireOp",EDGE,"E5.12.3.4"),sQuery(id+"F0.wireOp",EDGE,"E5.3.3.5"),sQuery(id+"F0.wireOp",EDGE,"E5.6.3.5"),sQuery(id+"F0.wireOp",EDGE,"E5.9.3.5"),sQuery(id+"F0.wireOp",EDGE,"E5.12.3.5"),sQuery(id+"F0.wireOp",EDGE,"E5.3.4.1"),sQuery(id+"F0.wireOp",EDGE,"E5.6.4.1"),sQuery(id+"F0.wireOp",EDGE,"E5.9.4.1"),sQuery(id+"F0.wireOp",EDGE,"E5.12.4.1"),sQuery(id+"F0.wireOp",EDGE,"E5.3.4.2"),sQuery(id+"F0.wireOp",EDGE,"E5.6.4.2"),sQuery(id+"F0.wireOp",EDGE,"E5.9.4.2"),sQuery(id+"F0.wireOp",EDGE,"E5.12.4.2"),sQuery(id+"F0.wireOp",EDGE,"E5.3.4.3"),sQuery(id+"F0.wireOp",EDGE,"E5.6.4.3"),sQuery(id+"F0.wireOp",EDGE,"E5.9.4.3"),sQuery(id+"F0.wireOp",EDGE,"E5.12.4.3"),sQuery(id+"F0.wireOp",EDGE,"E5.3.4.4"),sQuery(id+"F0.wireOp",EDGE,"E5.6.4.4"),sQuery(id+"F0.wireOp",EDGE,"E5.9.4.4"),sQuery(id+"F0.wireOp",EDGE,"E5.12.4.4"),sQuery(id+"F0.wireOp",EDGE,"E5.3.4.5"),sQuery(id+"F0.wireOp",EDGE,"E5.6.4.5"),sQuery(id+"F0.wireOp",EDGE,"E5.9.4.5"),sQuery(id+"F0.wireOp",EDGE,"E5.12.4.5"),sQuery(id+"F0.wireOp",EDGE,"E5.3.5.1"),sQuery(id+"F0.wireOp",EDGE,"E5.6.5.1"),sQuery(id+"F0.wireOp",EDGE,"E5.9.5.1"),sQuery(id+"F0.wireOp",EDGE,"E5.12.5.1"),sQuery(id+"F0.wireOp",EDGE,"E5.3.5.2"),sQuery(id+"F0.wireOp",EDGE,"E5.6.5.2"),sQuery(id+"F0.wireOp",EDGE,"E5.9.5.2"),sQuery(id+"F0.wireOp",EDGE,"E5.12.5.2"),sQuery(id+"F0.wireOp",EDGE,"E5.3.5.3"),sQuery(id+"F0.wireOp",EDGE,"E5.6.5.3"),sQuery(id+"F0.wireOp",EDGE,"E5.9.5.3"),sQuery(id+"F0.wireOp",EDGE,"E5.12.5.3"),sQuery(id+"F0.wireOp",EDGE,"E5.3.5.4"),sQuery(id+"F0.wireOp",EDGE,"E5.6.5.4"),sQuery(id+"F0.wireOp",EDGE,"E5.9.5.4"),sQuery(id+"F0.wireOp",EDGE,"E5.12.5.4"),sQuery(id+"F0.wireOp",EDGE,"E5.3.5.5"),sQuery(id+"F0.wireOp",EDGE,"E5.6.5.5"),sQuery(id+"F0.wireOp",EDGE,"E5.9.5.5"),sQuery(id+"F0.wireOp",EDGE,"E5.12.5.5"),sQuery(id+"F0.wireOp",EDGE,"E5.3.6.1"),sQuery(id+"F0.wireOp",EDGE,"E5.6.6.1"),sQuery(id+"F0.wireOp",EDGE,"E5.9.6.1"),sQuery(id+"F0.wireOp",EDGE,"E5.12.6.1"),sQuery(id+"F0.wireOp",EDGE,"E5.3.6.2"),sQuery(id+"F0.wireOp",EDGE,"E5.6.6.2"),sQuery(id+"F0.wireOp",EDGE,"E5.9.6.2"),sQuery(id+"F0.wireOp",EDGE,"E5.12.6.2"),sQuery(id+"F0.wireOp",EDGE,"E5.3.6.3"),sQuery(id+"F0.wireOp",EDGE,"E5.6.6.3"),sQuery(id+"F0.wireOp",EDGE,"E5.9.6.3"),sQuery(id+"F0.wireOp",EDGE,"E5.12.6.3"),sQuery(id+"F0.wireOp",EDGE,"E5.3.6.4"),sQuery(id+"F0.wireOp",EDGE,"E5.6.6.4"),sQuery(id+"F0.wireOp",EDGE,"E5.9.6.4"),sQuery(id+"F0.wireOp",EDGE,"E5.12.6.4"),sQuery(id+"F0.wireOp",EDGE,"E5.3.6.5"),sQuery(id+"F0.wireOp",EDGE,"E5.6.6.5"),sQuery(id+"F0.wireOp",EDGE,"E5.9.6.5"),sQuery(id+"F0.wireOp",EDGE,"E5.12.6.5"),sQuery(id+"F0.wireOp",EDGE,"E5.3.7.1"),sQuery(id+"F0.wireOp",EDGE,"E5.6.7.1"),sQuery(id+"F0.wireOp",EDGE,"E5.9.7.1"),sQuery(id+"F0.wireOp",EDGE,"E5.12.7.1"),sQuery(id+"F0.wireOp",EDGE,"E5.3.7.2"),sQuery(id+"F0.wireOp",EDGE,"E5.6.7.2"),sQuery(id+"F0.wireOp",EDGE,"E5.9.7.2"),sQuery(id+"F0.wireOp",EDGE,"E5.12.7.2"),sQuery(id+"F0.wireOp",EDGE,"E5.3.7.3"),sQuery(id+"F0.wireOp",EDGE,"E5.6.7.3"),sQuery(id+"F0.wireOp",EDGE,"E5.9.7.3"),sQuery(id+"F0.wireOp",EDGE,"E5.12.7.3"),sQuery(id+"F0.wireOp",EDGE,"E5.3.7.4"),sQuery(id+"F0.wireOp",EDGE,"E5.6.7.4"),sQuery(id+"F0.wireOp",EDGE,"E5.9.7.4"),sQuery(id+"F0.wireOp",EDGE,"E5.12.7.4"),sQuery(id+"F0.wireOp",EDGE,"E5.3.7.5"),sQuery(id+"F0.wireOp",EDGE,"E5.6.7.5"),sQuery(id+"F0.wireOp",EDGE,"E5.9.7.5"),sQuery(id+"F0.wireOp",EDGE,"E5.12.7.5"),sQuery(id+"F0.wireOp",EDGE,"E5.3.8.1"),sQuery(id+"F0.wireOp",EDGE,"E5.6.8.1"),sQuery(id+"F0.wireOp",EDGE,"E5.9.8.1"),sQuery(id+"F0.wireOp",EDGE,"E5.12.8.1"),sQuery(id+"F0.wireOp",EDGE,"E5.3.8.2"),sQuery(id+"F0.wireOp",EDGE,"E5.6.8.2"),sQuery(id+"F0.wireOp",EDGE,"E5.9.8.2"),sQuery(id+"F0.wireOp",EDGE,"E5.12.8.2"),sQuery(id+"F0.wireOp",EDGE,"E5.3.8.3"),sQuery(id+"F0.wireOp",EDGE,"E5.6.8.3"),sQuery(id+"F0.wireOp",EDGE,"E5.9.8.3"),sQuery(id+"F0.wireOp",EDGE,"E5.12.8.3"),sQuery(id+"F0.wireOp",EDGE,"E5.3.8.4"),sQuery(id+"F0.wireOp",EDGE,"E5.6.8.4"),sQuery(id+"F0.wireOp",EDGE,"E5.9.8.4"),sQuery(id+"F0.wireOp",EDGE,"E5.12.8.4"),sQuery(id+"F0.wireOp",EDGE,"E5.3.8.5"),sQuery(id+"F0.wireOp",EDGE,"E5.6.8.5"),sQuery(id+"F0.wireOp",EDGE,"E5.9.8.5"),sQuery(id+"F0.wireOp",EDGE,"E5.12.8.5"),sQuery(id+"F0.wireOp",EDGE,"E5.3.9.1"),sQuery(id+"F0.wireOp",EDGE,"E5.6.9.1"),sQuery(id+"F0.wireOp",EDGE,"E5.9.9.1"),sQuery(id+"F0.wireOp",EDGE,"E5.12.9.1"),sQuery(id+"F0.wireOp",EDGE,"E5.3.9.2"),sQuery(id+"F0.wireOp",EDGE,"E5.6.9.2"),sQuery(id+"F0.wireOp",EDGE,"E5.9.9.2"),sQuery(id+"F0.wireOp",EDGE,"E5.12.9.2"),sQuery(id+"F0.wireOp",EDGE,"E5.3.9.3"),sQuery(id+"F0.wireOp",EDGE,"E5.6.9.3"),sQuery(id+"F0.wireOp",EDGE,"E5.9.9.3"),sQuery(id+"F0.wireOp",EDGE,"E5.12.9.3"),sQuery(id+"F0.wireOp",EDGE,"E5.3.9.4"),sQuery(id+"F0.wireOp",EDGE,"E5.6.9.4"),sQuery(id+"F0.wireOp",EDGE,"E5.9.9.4"),sQuery(id+"F0.wireOp",EDGE,"E5.12.9.4"),sQuery(id+"F0.wireOp",EDGE,"E5.3.9.5"),sQuery(id+"F0.wireOp",EDGE,"E5.6.9.5"),sQuery(id+"F0.wireOp",EDGE,"E5.9.9.5"),sQuery(id+"F0.wireOp",EDGE,"E5.12.9.5"),sQuery(id+"F0.wireOp",EDGE,"E5.3.10.1"),sQuery(id+"F0.wireOp",EDGE,"E5.6.10.1"),sQuery(id+"F0.wireOp",EDGE,"E5.9.10.1"),sQuery(id+"F0.wireOp",EDGE,"E5.12.10.1"),sQuery(id+"F0.wireOp",EDGE,"E5.3.10.2"),sQuery(id+"F0.wireOp",EDGE,"E5.6.10.2"),sQuery(id+"F0.wireOp",EDGE,"E5.9.10.2"),sQuery(id+"F0.wireOp",EDGE,"E5.12.10.2"),sQuery(id+"F0.wireOp",EDGE,"E5.3.10.3"),sQuery(id+"F0.wireOp",EDGE,"E5.6.10.3"),sQuery(id+"F0.wireOp",EDGE,"E5.9.10.3"),sQuery(id+"F0.wireOp",EDGE,"E5.12.10.3"),sQuery(id+"F0.wireOp",EDGE,"E5.3.10.4"),sQuery(id+"F0.wireOp",EDGE,"E5.6.10.4"),sQuery(id+"F0.wireOp",EDGE,"E5.9.10.4"),sQuery(id+"F0.wireOp",EDGE,"E5.12.10.4"),sQuery(id+"F0.wireOp",EDGE,"E5.3.10.5"),sQuery(id+"F0.wireOp",EDGE,"E5.6.10.5"),sQuery(id+"F0.wireOp",EDGE,"E5.9.10.5"),sQuery(id+"F0.wireOp",EDGE,"E5.12.10.5"),sQuery(id+"F0.wireOp",EDGE,"E5.3.11.1"),sQuery(id+"F0.wireOp",EDGE,"E5.6.11.1"),sQuery(id+"F0.wireOp",EDGE,"E5.9.11.1"),sQuery(id+"F0.wireOp",EDGE,"E5.12.11.1"),sQuery(id+"F0.wireOp",EDGE,"E5.3.11.2"),sQuery(id+"F0.wireOp",EDGE,"E5.6.11.2"),sQuery(id+"F0.wireOp",EDGE,"E5.9.11.2"),sQuery(id+"F0.wireOp",EDGE,"E5.12.11.2"),sQuery(id+"F0.wireOp",EDGE,"E5.3.11.3"),sQuery(id+"F0.wireOp",EDGE,"E5.6.11.3"),sQuery(id+"F0.wireOp",EDGE,"E5.9.11.3"),sQuery(id+"F0.wireOp",EDGE,"E5.12.11.3"),sQuery(id+"F0.wireOp",EDGE,"E5.3.11.4"),sQuery(id+"F0.wireOp",EDGE,"E5.6.11.4"),sQuery(id+"F0.wireOp",EDGE,"E5.9.11.4"),sQuery(id+"F0.wireOp",EDGE,"E5.12.11.4"),sQuery(id+"F0.wireOp",EDGE,"E5.3.11.5"),sQuery(id+"F0.wireOp",EDGE,"E5.6.11.5"),sQuery(id+"F0.wireOp",EDGE,"E5.9.11.5"),sQuery(id+"F0.wireOp",EDGE,"E5.12.11.5"),sQuery(id+"F0.wireOp",EDGE,"E6.bottom"),sQuery(id+"F0.wireOp",EDGE,"E6.top"),sQuery(id+"F0.wireOp",EDGE,"E6.left"),sQuery(id+"F0.wireOp",EDGE,"E6.right"),sQuery(id+"F0.wireOp",EDGE,"E7.0.1.0"),sQuery(id+"F0.wireOp",EDGE,"E7.0.1.1"),sQuery(id+"F0.wireOp",EDGE,"E7.0.1.2"),sQuery(id+"F0.wireOp",EDGE,"E7.0.1.3"),sQuery(id+"F0.wireOp",EDGE,"E7.0.2.0"),sQuery(id+"F0.wireOp",EDGE,"E7.0.2.1"),sQuery(id+"F0.wireOp",EDGE,"E7.0.2.2"),sQuery(id+"F0.wireOp",EDGE,"E7.0.2.3"),sQuery(id+"F0.wireOp",EDGE,"E7.0.3.0"),sQuery(id+"F0.wireOp",EDGE,"E7.0.3.1"),sQuery(id+"F0.wireOp",EDGE,"E7.0.3.2"),sQuery(id+"F0.wireOp",EDGE,"E7.0.3.3"),sQuery(id+"F0.wireOp",EDGE,"E7.0.4.0"),sQuery(id+"F0.wireOp",EDGE,"E7.0.4.1"),sQuery(id+"F0.wireOp",EDGE,"E7.0.4.2"),sQuery(id+"F0.wireOp",EDGE,"E7.0.4.3"),sQuery(id+"F0.wireOp",EDGE,"E7.0.5.0"),sQuery(id+"F0.wireOp",EDGE,"E7.0.5.1"),sQuery(id+"F0.wireOp",EDGE,"E7.0.5.2"),sQuery(id+"F0.wireOp",EDGE,"E7.0.5.3"),sQuery(id+"F0.wireOp",EDGE,"E7.1.0.0"),sQuery(id+"F0.wireOp",EDGE,"E7.1.0.1"),sQuery(id+"F0.wireOp",EDGE,"E7.1.0.2"),sQuery(id+"F0.wireOp",EDGE,"E7.1.0.3"),sQuery(id+"F0.wireOp",EDGE,"E7.1.1.0"),sQuery(id+"F0.wireOp",EDGE,"E7.1.1.1"),sQuery(id+"F0.wireOp",EDGE,"E7.1.1.2"),sQuery(id+"F0.wireOp",EDGE,"E7.1.1.3"),sQuery(id+"F0.wireOp",EDGE,"E7.1.2.0"),sQuery(id+"F0.wireOp",EDGE,"E7.1.2.1"),sQuery(id+"F0.wireOp",EDGE,"E7.1.2.2"),sQuery(id+"F0.wireOp",EDGE,"E7.1.2.3"),sQuery(id+"F0.wireOp",EDGE,"E7.1.3.0"),sQuery(id+"F0.wireOp",EDGE,"E7.1.3.1"),sQuery(id+"F0.wireOp",EDGE,"E7.1.3.2"),sQuery(id+"F0.wireOp",EDGE,"E7.1.3.3"),sQuery(id+"F0.wireOp",EDGE,"E7.1.4.0"),sQuery(id+"F0.wireOp",EDGE,"E7.1.4.1"),sQuery(id+"F0.wireOp",EDGE,"E7.1.4.2"),sQuery(id+"F0.wireOp",EDGE,"E7.1.4.3"),sQuery(id+"F0.wireOp",EDGE,"E7.1.5.0"),sQuery(id+"F0.wireOp",EDGE,"E7.1.5.1"),sQuery(id+"F0.wireOp",EDGE,"E7.1.5.2"),sQuery(id+"F0.wireOp",EDGE,"E7.1.5.3"),sQuery(id+"F0.wireOp",EDGE,"E7.2.0.0"),sQuery(id+"F0.wireOp",EDGE,"E7.2.0.1"),sQuery(id+"F0.wireOp",EDGE,"E7.2.0.2"),sQuery(id+"F0.wireOp",EDGE,"E7.2.0.3"),sQuery(id+"F0.wireOp",EDGE,"E7.2.1.0"),sQuery(id+"F0.wireOp",EDGE,"E7.2.1.1"),sQuery(id+"F0.wireOp",EDGE,"E7.2.1.2"),sQuery(id+"F0.wireOp",EDGE,"E7.2.1.3"),sQuery(id+"F0.wireOp",EDGE,"E7.2.2.0"),sQuery(id+"F0.wireOp",EDGE,"E7.2.2.1"),sQuery(id+"F0.wireOp",EDGE,"E7.2.2.2"),sQuery(id+"F0.wireOp",EDGE,"E7.2.2.3"),sQuery(id+"F0.wireOp",EDGE,"E7.2.3.0"),sQuery(id+"F0.wireOp",EDGE,"E7.2.3.1"),sQuery(id+"F0.wireOp",EDGE,"E7.2.3.2"),sQuery(id+"F0.wireOp",EDGE,"E7.2.3.3"),sQuery(id+"F0.wireOp",EDGE,"E7.2.4.0"),sQuery(id+"F0.wireOp",EDGE,"E7.2.4.1"),sQuery(id+"F0.wireOp",EDGE,"E7.2.4.2"),sQuery(id+"F0.wireOp",EDGE,"E7.2.4.3"),sQuery(id+"F0.wireOp",EDGE,"E7.2.5.0"),sQuery(id+"F0.wireOp",EDGE,"E7.2.5.1"),sQuery(id+"F0.wireOp",EDGE,"E7.2.5.2"),sQuery(id+"F0.wireOp",EDGE,"E7.2.5.3"),sQuery(id+"F0.wireOp",EDGE,"E7.3.0.0"),sQuery(id+"F0.wireOp",EDGE,"E7.3.0.1"),sQuery(id+"F0.wireOp",EDGE,"E7.3.0.2"),sQuery(id+"F0.wireOp",EDGE,"E7.3.0.3"),sQuery(id+"F0.wireOp",EDGE,"E7.3.1.0"),sQuery(id+"F0.wireOp",EDGE,"E7.3.1.1"),sQuery(id+"F0.wireOp",EDGE,"E7.3.1.2"),sQuery(id+"F0.wireOp",EDGE,"E7.3.1.3"),sQuery(id+"F0.wireOp",EDGE,"E7.3.2.0"),sQuery(id+"F0.wireOp",EDGE,"E7.3.2.1"),sQuery(id+"F0.wireOp",EDGE,"E7.3.2.2"),sQuery(id+"F0.wireOp",EDGE,"E7.3.2.3"),sQuery(id+"F0.wireOp",EDGE,"E7.3.3.0"),sQuery(id+"F0.wireOp",EDGE,"E7.3.3.1"),sQuery(id+"F0.wireOp",EDGE,"E7.3.3.2"),sQuery(id+"F0.wireOp",EDGE,"E7.3.3.3"),sQuery(id+"F0.wireOp",EDGE,"E7.3.4.0"),sQuery(id+"F0.wireOp",EDGE,"E7.3.4.1"),sQuery(id+"F0.wireOp",EDGE,"E7.3.4.2"),sQuery(id+"F0.wireOp",EDGE,"E7.3.4.3"),sQuery(id+"F0.wireOp",EDGE,"E7.3.5.0"),sQuery(id+"F0.wireOp",EDGE,"E7.3.5.1"),sQuery(id+"F0.wireOp",EDGE,"E7.3.5.2"),sQuery(id+"F0.wireOp",EDGE,"E7.3.5.3"),sQuery(id+"F0.wireOp",EDGE,"E7.4.0.0"),sQuery(id+"F0.wireOp",EDGE,"E7.4.0.1"),sQuery(id+"F0.wireOp",EDGE,"E7.4.0.2"),sQuery(id+"F0.wireOp",EDGE,"E7.4.0.3"),sQuery(id+"F0.wireOp",EDGE,"E7.4.1.0"),sQuery(id+"F0.wireOp",EDGE,"E7.4.1.1"),sQuery(id+"F0.wireOp",EDGE,"E7.4.1.2"),sQuery(id+"F0.wireOp",EDGE,"E7.4.1.3"),sQuery(id+"F0.wireOp",EDGE,"E7.4.2.0"),sQuery(id+"F0.wireOp",EDGE,"E7.4.2.1"),sQuery(id+"F0.wireOp",EDGE,"E7.4.2.2"),sQuery(id+"F0.wireOp",EDGE,"E7.4.2.3"),sQuery(id+"F0.wireOp",EDGE,"E7.4.3.0"),sQuery(id+"F0.wireOp",EDGE,"E7.4.3.1"),sQuery(id+"F0.wireOp",EDGE,"E7.4.3.2"),sQuery(id+"F0.wireOp",EDGE,"E7.4.3.3"),sQuery(id+"F0.wireOp",EDGE,"E7.4.4.0"),sQuery(id+"F0.wireOp",EDGE,"E7.4.4.1"),sQuery(id+"F0.wireOp",EDGE,"E7.4.4.2"),sQuery(id+"F0.wireOp",EDGE,"E7.4.4.3"),sQuery(id+"F0.wireOp",EDGE,"E7.4.5.0"),sQuery(id+"F0.wireOp",EDGE,"E7.4.5.1"),sQuery(id+"F0.wireOp",EDGE,"E7.4.5.2"),sQuery(id+"F0.wireOp",EDGE,"E7.4.5.3"),sQuery(id+"F0.wireOp",EDGE,"E7.5.0.0"),sQuery(id+"F0.wireOp",EDGE,"E7.5.0.1"),sQuery(id+"F0.wireOp",EDGE,"E7.5.0.2"),sQuery(id+"F0.wireOp",EDGE,"E7.5.0.3"),sQuery(id+"F0.wireOp",EDGE,"E7.5.1.0"),sQuery(id+"F0.wireOp",EDGE,"E7.5.1.1"),sQuery(id+"F0.wireOp",EDGE,"E7.5.1.2"),sQuery(id+"F0.wireOp",EDGE,"E7.5.1.3"),sQuery(id+"F0.wireOp",EDGE,"E7.5.2.0"),sQuery(id+"F0.wireOp",EDGE,"E7.5.2.1"),sQuery(id+"F0.wireOp",EDGE,"E7.5.2.2"),sQuery(id+"F0.wireOp",EDGE,"E7.5.2.3"),sQuery(id+"F0.wireOp",EDGE,"E7.5.3.0"),sQuery(id+"F0.wireOp",EDGE,"E7.5.3.1"),sQuery(id+"F0.wireOp",EDGE,"E7.5.3.2"),sQuery(id+"F0.wireOp",EDGE,"E7.5.3.3"),sQuery(id+"F0.wireOp",EDGE,"E7.5.4.0"),sQuery(id+"F0.wireOp",EDGE,"E7.5.4.1"),sQuery(id+"F0.wireOp",EDGE,"E7.5.4.2"),sQuery(id+"F0.wireOp",EDGE,"E7.5.4.3"),sQuery(id+"F0.wireOp",EDGE,"E7.5.5.0"),sQuery(id+"F0.wireOp",EDGE,"E7.5.5.1"),sQuery(id+"F0.wireOp",EDGE,"E7.5.5.2"),sQuery(id+"F0.wireOp",EDGE,"E7.5.5.3"),sQuery(id+"F0.wireOp",EDGE,"E7.6.0.0"),sQuery(id+"F0.wireOp",EDGE,"E7.6.0.1"),sQuery(id+"F0.wireOp",EDGE,"E7.6.0.2"),sQuery(id+"F0.wireOp",EDGE,"E7.6.0.3"),sQuery(id+"F0.wireOp",EDGE,"E7.6.1.0"),sQuery(id+"F0.wireOp",EDGE,"E7.6.1.1"),sQuery(id+"F0.wireOp",EDGE,"E7.6.1.2"),sQuery(id+"F0.wireOp",EDGE,"E7.6.1.3"),sQuery(id+"F0.wireOp",EDGE,"E7.6.2.0"),sQuery(id+"F0.wireOp",EDGE,"E7.6.2.1"),sQuery(id+"F0.wireOp",EDGE,"E7.6.2.2"),sQuery(id+"F0.wireOp",EDGE,"E7.6.2.3"),sQuery(id+"F0.wireOp",EDGE,"E7.6.3.0"),sQuery(id+"F0.wireOp",EDGE,"E7.6.3.1"),sQuery(id+"F0.wireOp",EDGE,"E7.6.3.2"),sQuery(id+"F0.wireOp",EDGE,"E7.6.3.3"),sQuery(id+"F0.wireOp",EDGE,"E7.6.4.0"),sQuery(id+"F0.wireOp",EDGE,"E7.6.4.1"),sQuery(id+"F0.wireOp",EDGE,"E7.6.4.2"),sQuery(id+"F0.wireOp",EDGE,"E7.6.4.3"),sQuery(id+"F0.wireOp",EDGE,"E7.6.5.0"),sQuery(id+"F0.wireOp",EDGE,"E7.6.5.1"),sQuery(id+"F0.wireOp",EDGE,"E7.6.5.2"),sQuery(id+"F0.wireOp",EDGE,"E7.6.5.3"),sQuery(id+"F0.wireOp",EDGE,"E7.7.0.0"),sQuery(id+"F0.wireOp",EDGE,"E7.7.0.1"),sQuery(id+"F0.wireOp",EDGE,"E7.7.0.2"),sQuery(id+"F0.wireOp",EDGE,"E7.7.0.3"),sQuery(id+"F0.wireOp",EDGE,"E7.7.1.0"),sQuery(id+"F0.wireOp",EDGE,"E7.7.1.1"),sQuery(id+"F0.wireOp",EDGE,"E7.7.1.2"),sQuery(id+"F0.wireOp",EDGE,"E7.7.1.3"),sQuery(id+"F0.wireOp",EDGE,"E7.7.2.0"),sQuery(id+"F0.wireOp",EDGE,"E7.7.2.1"),sQuery(id+"F0.wireOp",EDGE,"E7.7.2.2"),sQuery(id+"F0.wireOp",EDGE,"E7.7.2.3"),sQuery(id+"F0.wireOp",EDGE,"E7.7.3.0"),sQuery(id+"F0.wireOp",EDGE,"E7.7.3.1"),sQuery(id+"F0.wireOp",EDGE,"E7.7.3.2"),sQuery(id+"F0.wireOp",EDGE,"E7.7.3.3"),sQuery(id+"F0.wireOp",EDGE,"E7.7.4.0"),sQuery(id+"F0.wireOp",EDGE,"E7.7.4.1"),sQuery(id+"F0.wireOp",EDGE,"E7.7.4.2"),sQuery(id+"F0.wireOp",EDGE,"E7.7.4.3"),sQuery(id+"F0.wireOp",EDGE,"E7.7.5.0"),sQuery(id+"F0.wireOp",EDGE,"E7.7.5.1"),sQuery(id+"F0.wireOp",EDGE,"E7.7.5.2"),sQuery(id+"F0.wireOp",EDGE,"E7.7.5.3"),sQuery(id+"F0.wireOp",EDGE,"E7.8.0.0"),sQuery(id+"F0.wireOp",EDGE,"E7.8.0.1"),sQuery(id+"F0.wireOp",EDGE,"E7.8.0.2"),sQuery(id+"F0.wireOp",EDGE,"E7.8.0.3"),sQuery(id+"F0.wireOp",EDGE,"E7.8.1.0"),sQuery(id+"F0.wireOp",EDGE,"E7.8.1.1"),sQuery(id+"F0.wireOp",EDGE,"E7.8.1.2"),sQuery(id+"F0.wireOp",EDGE,"E7.8.1.3"),sQuery(id+"F0.wireOp",EDGE,"E7.8.2.0"),sQuery(id+"F0.wireOp",EDGE,"E7.8.2.1"),sQuery(id+"F0.wireOp",EDGE,"E7.8.2.2"),sQuery(id+"F0.wireOp",EDGE,"E7.8.2.3"),sQuery(id+"F0.wireOp",EDGE,"E7.8.3.0"),sQuery(id+"F0.wireOp",EDGE,"E7.8.3.1"),sQuery(id+"F0.wireOp",EDGE,"E7.8.3.2"),sQuery(id+"F0.wireOp",EDGE,"E7.8.3.3"),sQuery(id+"F0.wireOp",EDGE,"E7.8.4.0"),sQuery(id+"F0.wireOp",EDGE,"E7.8.4.1"),sQuery(id+"F0.wireOp",EDGE,"E7.8.4.2"),sQuery(id+"F0.wireOp",EDGE,"E7.8.4.3"),sQuery(id+"F0.wireOp",EDGE,"E7.8.5.0"),sQuery(id+"F0.wireOp",EDGE,"E7.8.5.1"),sQuery(id+"F0.wireOp",EDGE,"E7.8.5.2"),sQuery(id+"F0.wireOp",EDGE,"E7.8.5.3"),sQuery(id+"F0.wireOp",EDGE,"E7.9.0.0"),sQuery(id+"F0.wireOp",EDGE,"E7.9.0.1"),sQuery(id+"F0.wireOp",EDGE,"E7.9.0.2"),sQuery(id+"F0.wireOp",EDGE,"E7.9.0.3"),sQuery(id+"F0.wireOp",EDGE,"E7.9.1.0"),sQuery(id+"F0.wireOp",EDGE,"E7.9.1.1"),sQuery(id+"F0.wireOp",EDGE,"E7.9.1.2"),sQuery(id+"F0.wireOp",EDGE,"E7.9.1.3"),sQuery(id+"F0.wireOp",EDGE,"E7.9.2.0"),sQuery(id+"F0.wireOp",EDGE,"E7.9.2.1"),sQuery(id+"F0.wireOp",EDGE,"E7.9.2.2"),sQuery(id+"F0.wireOp",EDGE,"E7.9.2.3"),sQuery(id+"F0.wireOp",EDGE,"E7.9.3.0"),sQuery(id+"F0.wireOp",EDGE,"E7.9.3.1"),sQuery(id+"F0.wireOp",EDGE,"E7.9.3.2"),sQuery(id+"F0.wireOp",EDGE,"E7.9.3.3"),sQuery(id+"F0.wireOp",EDGE,"E7.9.4.0"),sQuery(id+"F0.wireOp",EDGE,"E7.9.4.1"),sQuery(id+"F0.wireOp",EDGE,"E7.9.4.2"),sQuery(id+"F0.wireOp",EDGE,"E7.9.4.3"),sQuery(id+"F0.wireOp",EDGE,"E7.9.5.0"),sQuery(id+"F0.wireOp",EDGE,"E7.9.5.1"),sQuery(id+"F0.wireOp",EDGE,"E7.9.5.2"),sQuery(id+"F0.wireOp",EDGE,"E7.9.5.3"),sQuery(id+"F0.wireOp",EDGE,"E7.10.0.0"),sQuery(id+"F0.wireOp",EDGE,"E7.10.0.1"),sQuery(id+"F0.wireOp",EDGE,"E7.10.0.2"),sQuery(id+"F0.wireOp",EDGE,"E7.10.0.3"),sQuery(id+"F0.wireOp",EDGE,"E7.10.1.0"),sQuery(id+"F0.wireOp",EDGE,"E7.10.1.1"),sQuery(id+"F0.wireOp",EDGE,"E7.10.1.2"),sQuery(id+"F0.wireOp",EDGE,"E7.10.1.3"),sQuery(id+"F0.wireOp",EDGE,"E7.10.2.0"),sQuery(id+"F0.wireOp",EDGE,"E7.10.2.1"),sQuery(id+"F0.wireOp",EDGE,"E7.10.2.2"),sQuery(id+"F0.wireOp",EDGE,"E7.10.2.3"),sQuery(id+"F0.wireOp",EDGE,"E7.10.3.0"),sQuery(id+"F0.wireOp",EDGE,"E7.10.3.1"),sQuery(id+"F0.wireOp",EDGE,"E7.10.3.2"),sQuery(id+"F0.wireOp",EDGE,"E7.10.3.3"),sQuery(id+"F0.wireOp",EDGE,"E7.10.4.0"),sQuery(id+"F0.wireOp",EDGE,"E7.10.4.1"),sQuery(id+"F0.wireOp",EDGE,"E7.10.4.2"),sQuery(id+"F0.wireOp",EDGE,"E7.10.4.3"),sQuery(id+"F0.wireOp",EDGE,"E7.10.5.0"),sQuery(id+"F0.wireOp",EDGE,"E7.10.5.1"),sQuery(id+"F0.wireOp",EDGE,"E7.10.5.2"),sQuery(id+"F0.wireOp",EDGE,"E7.10.5.3"),sQuery(id+"F0.wireOp",EDGE,"E7.11.0.0"),sQuery(id+"F0.wireOp",EDGE,"E7.11.0.1"),sQuery(id+"F0.wireOp",EDGE,"E7.11.0.2"),sQuery(id+"F0.wireOp",EDGE,"E7.11.0.3"),sQuery(id+"F0.wireOp",EDGE,"E7.11.1.0"),sQuery(id+"F0.wireOp",EDGE,"E7.11.1.1"),sQuery(id+"F0.wireOp",EDGE,"E7.11.1.2"),sQuery(id+"F0.wireOp",EDGE,"E7.11.1.3"),sQuery(id+"F0.wireOp",EDGE,"E7.11.2.0"),sQuery(id+"F0.wireOp",EDGE,"E7.11.2.1"),sQuery(id+"F0.wireOp",EDGE,"E7.11.2.2"),sQuery(id+"F0.wireOp",EDGE,"E7.11.2.3"),sQuery(id+"F0.wireOp",EDGE,"E7.11.3.0"),sQuery(id+"F0.wireOp",EDGE,"E7.11.3.1"),sQuery(id+"F0.wireOp",EDGE,"E7.11.3.2"),sQuery(id+"F0.wireOp",EDGE,"E7.11.3.3"),sQuery(id+"F0.wireOp",EDGE,"E7.11.4.0"),sQuery(id+"F0.wireOp",EDGE,"E7.11.4.1"),sQuery(id+"F0.wireOp",EDGE,"E7.11.4.2"),sQuery(id+"F0.wireOp",EDGE,"E7.11.4.3"),sQuery(id+"F0.wireOp",EDGE,"E7.11.5.0"),sQuery(id+"F0.wireOp",EDGE,"E7.11.5.1"),sQuery(id+"F0.wireOp",EDGE,"E7.11.5.2"),sQuery(id+"F0.wireOp",EDGE,"E7.11.5.3")])],"isStart":false});
            var Q1;
            Q1=makeQuery(id+"F1.opExtrude","CAP_FACE",FACE,{"disambiguationData":[OSD([sQuery(id+"F0.wireOp",EDGE,"E0.bottom"),sQuery(id+"F0.wireOp",EDGE,"E0.top"),sQuery(id+"F0.wireOp",EDGE,"E0.left"),sQuery(id+"F0.wireOp",EDGE,"E0.right"),sQuery(id+"F0.wireOp",EDGE,"E1.bottom"),sQuery(id+"F0.wireOp",EDGE,"E1.top"),sQuery(id+"F0.wireOp",EDGE,"E1.left"),sQuery(id+"F0.wireOp",EDGE,"E1.right"),sQuery(id+"F0.wireOp",EDGE,"E4.3.1.0"),sQuery(id+"F0.wireOp",EDGE,"E4.6.1.0"),sQuery(id+"F0.wireOp",EDGE,"E4.9.1.0"),sQuery(id+"F0.wireOp",EDGE,"E4.12.1.0"),sQuery(id+"F0.wireOp",EDGE,"E4.3.2.0"),sQuery(id+"F0.wireOp",EDGE,"E4.6.2.0"),sQuery(id+"F0.wireOp",EDGE,"E4.9.2.0"),sQuery(id+"F0.wireOp",EDGE,"E4.12.2.0"),sQuery(id+"F0.wireOp",EDGE,"E4.3.3.0"),sQuery(id+"F0.wireOp",EDGE,"E4.6.3.0"),sQuery(id+"F0.wireOp",EDGE,"E4.9.3.0"),sQuery(id+"F0.wireOp",EDGE,"E4.12.3.0"),sQuery(id+"F0.wireOp",EDGE,"E4.3.4.0"),sQuery(id+"F0.wireOp",EDGE,"E4.6.4.0"),sQuery(id+"F0.wireOp",EDGE,"E4.9.4.0"),sQuery(id+"F0.wireOp",EDGE,"E4.12.4.0"),sQuery(id+"F0.wireOp",EDGE,"E4.3.5.0"),sQuery(id+"F0.wireOp",EDGE,"E4.6.5.0"),sQuery(id+"F0.wireOp",EDGE,"E4.9.5.0"),sQuery(id+"F0.wireOp",EDGE,"E4.12.5.0"),sQuery(id+"F0.wireOp",EDGE,"E4.3.6.0"),sQuery(id+"F0.wireOp",EDGE,"E4.6.6.0"),sQuery(id+"F0.wireOp",EDGE,"E4.9.6.0"),sQuery(id+"F0.wireOp",EDGE,"E4.12.6.0"),sQuery(id+"F0.wireOp",EDGE,"E4.3.7.0"),sQuery(id+"F0.wireOp",EDGE,"E4.6.7.0"),sQuery(id+"F0.wireOp",EDGE,"E4.9.7.0"),sQuery(id+"F0.wireOp",EDGE,"E4.12.7.0"),sQuery(id+"F0.wireOp",EDGE,"E4.3.8.0"),sQuery(id+"F0.wireOp",EDGE,"E4.6.8.0"),sQuery(id+"F0.wireOp",EDGE,"E4.9.8.0"),sQuery(id+"F0.wireOp",EDGE,"E4.12.8.0"),sQuery(id+"F0.wireOp",EDGE,"E4.3.9.0"),sQuery(id+"F0.wireOp",EDGE,"E4.6.9.0"),sQuery(id+"F0.wireOp",EDGE,"E4.9.9.0"),sQuery(id+"F0.wireOp",EDGE,"E4.12.9.0"),sQuery(id+"F0.wireOp",EDGE,"E4.3.10.0"),sQuery(id+"F0.wireOp",EDGE,"E4.6.10.0"),sQuery(id+"F0.wireOp",EDGE,"E4.9.10.0"),sQuery(id+"F0.wireOp",EDGE,"E4.12.10.0"),sQuery(id+"F0.wireOp",EDGE,"E4.3.11.0"),sQuery(id+"F0.wireOp",EDGE,"E4.6.11.0"),sQuery(id+"F0.wireOp",EDGE,"E4.9.11.0"),sQuery(id+"F0.wireOp",EDGE,"E4.12.11.0"),sQuery(id+"F0.wireOp",EDGE,"E5.3.0.1"),sQuery(id+"F0.wireOp",EDGE,"E5.6.0.1"),sQuery(id+"F0.wireOp",EDGE,"E5.9.0.1"),sQuery(id+"F0.wireOp",EDGE,"E5.12.0.1"),sQuery(id+"F0.wireOp",EDGE,"E5.3.0.2"),sQuery(id+"F0.wireOp",EDGE,"E5.6.0.2"),sQuery(id+"F0.wireOp",EDGE,"E5.9.0.2"),sQuery(id+"F0.wireOp",EDGE,"E5.12.0.2"),sQuery(id+"F0.wireOp",EDGE,"E5.3.0.3"),sQuery(id+"F0.wireOp",EDGE,"E5.6.0.3"),sQuery(id+"F0.wireOp",EDGE,"E5.9.0.3"),sQuery(id+"F0.wireOp",EDGE,"E5.12.0.3"),sQuery(id+"F0.wireOp",EDGE,"E5.3.0.4"),sQuery(id+"F0.wireOp",EDGE,"E5.6.0.4"),sQuery(id+"F0.wireOp",EDGE,"E5.9.0.4"),sQuery(id+"F0.wireOp",EDGE,"E5.12.0.4"),sQuery(id+"F0.wireOp",EDGE,"E5.3.0.5"),sQuery(id+"F0.wireOp",EDGE,"E5.6.0.5"),sQuery(id+"F0.wireOp",EDGE,"E5.9.0.5"),sQuery(id+"F0.wireOp",EDGE,"E5.12.0.5"),sQuery(id+"F0.wireOp",EDGE,"E5.3.1.1"),sQuery(id+"F0.wireOp",EDGE,"E5.6.1.1"),sQuery(id+"F0.wireOp",EDGE,"E5.9.1.1"),sQuery(id+"F0.wireOp",EDGE,"E5.12.1.1"),sQuery(id+"F0.wireOp",EDGE,"E5.3.1.2"),sQuery(id+"F0.wireOp",EDGE,"E5.6.1.2"),sQuery(id+"F0.wireOp",EDGE,"E5.9.1.2"),sQuery(id+"F0.wireOp",EDGE,"E5.12.1.2"),sQuery(id+"F0.wireOp",EDGE,"E5.3.1.3"),sQuery(id+"F0.wireOp",EDGE,"E5.6.1.3"),sQuery(id+"F0.wireOp",EDGE,"E5.9.1.3"),sQuery(id+"F0.wireOp",EDGE,"E5.12.1.3"),sQuery(id+"F0.wireOp",EDGE,"E5.3.1.4"),sQuery(id+"F0.wireOp",EDGE,"E5.6.1.4"),sQuery(id+"F0.wireOp",EDGE,"E5.9.1.4"),sQuery(id+"F0.wireOp",EDGE,"E5.12.1.4"),sQuery(id+"F0.wireOp",EDGE,"E5.3.1.5"),sQuery(id+"F0.wireOp",EDGE,"E5.6.1.5"),sQuery(id+"F0.wireOp",EDGE,"E5.9.1.5"),sQuery(id+"F0.wireOp",EDGE,"E5.12.1.5"),sQuery(id+"F0.wireOp",EDGE,"E5.3.2.1"),sQuery(id+"F0.wireOp",EDGE,"E5.6.2.1"),sQuery(id+"F0.wireOp",EDGE,"E5.9.2.1"),sQuery(id+"F0.wireOp",EDGE,"E5.12.2.1"),sQuery(id+"F0.wireOp",EDGE,"E5.3.2.2"),sQuery(id+"F0.wireOp",EDGE,"E5.6.2.2"),sQuery(id+"F0.wireOp",EDGE,"E5.9.2.2"),sQuery(id+"F0.wireOp",EDGE,"E5.12.2.2"),sQuery(id+"F0.wireOp",EDGE,"E5.3.2.3"),sQuery(id+"F0.wireOp",EDGE,"E5.6.2.3"),sQuery(id+"F0.wireOp",EDGE,"E5.9.2.3"),sQuery(id+"F0.wireOp",EDGE,"E5.12.2.3"),sQuery(id+"F0.wireOp",EDGE,"E5.3.2.4"),sQuery(id+"F0.wireOp",EDGE,"E5.6.2.4"),sQuery(id+"F0.wireOp",EDGE,"E5.9.2.4"),sQuery(id+"F0.wireOp",EDGE,"E5.12.2.4"),sQuery(id+"F0.wireOp",EDGE,"E5.3.2.5"),sQuery(id+"F0.wireOp",EDGE,"E5.6.2.5"),sQuery(id+"F0.wireOp",EDGE,"E5.9.2.5"),sQuery(id+"F0.wireOp",EDGE,"E5.12.2.5"),sQuery(id+"F0.wireOp",EDGE,"E5.3.3.1"),sQuery(id+"F0.wireOp",EDGE,"E5.6.3.1"),sQuery(id+"F0.wireOp",EDGE,"E5.9.3.1"),sQuery(id+"F0.wireOp",EDGE,"E5.12.3.1"),sQuery(id+"F0.wireOp",EDGE,"E5.3.3.2"),sQuery(id+"F0.wireOp",EDGE,"E5.6.3.2"),sQuery(id+"F0.wireOp",EDGE,"E5.9.3.2"),sQuery(id+"F0.wireOp",EDGE,"E5.12.3.2"),sQuery(id+"F0.wireOp",EDGE,"E5.3.3.3"),sQuery(id+"F0.wireOp",EDGE,"E5.6.3.3"),sQuery(id+"F0.wireOp",EDGE,"E5.9.3.3"),sQuery(id+"F0.wireOp",EDGE,"E5.12.3.3"),sQuery(id+"F0.wireOp",EDGE,"E5.3.3.4"),sQuery(id+"F0.wireOp",EDGE,"E5.6.3.4"),sQuery(id+"F0.wireOp",EDGE,"E5.9.3.4"),sQuery(id+"F0.wireOp",EDGE,"E5.12.3.4"),sQuery(id+"F0.wireOp",EDGE,"E5.3.3.5"),sQuery(id+"F0.wireOp",EDGE,"E5.6.3.5"),sQuery(id+"F0.wireOp",EDGE,"E5.9.3.5"),sQuery(id+"F0.wireOp",EDGE,"E5.12.3.5"),sQuery(id+"F0.wireOp",EDGE,"E5.3.4.1"),sQuery(id+"F0.wireOp",EDGE,"E5.6.4.1"),sQuery(id+"F0.wireOp",EDGE,"E5.9.4.1"),sQuery(id+"F0.wireOp",EDGE,"E5.12.4.1"),sQuery(id+"F0.wireOp",EDGE,"E5.3.4.2"),sQuery(id+"F0.wireOp",EDGE,"E5.6.4.2"),sQuery(id+"F0.wireOp",EDGE,"E5.9.4.2"),sQuery(id+"F0.wireOp",EDGE,"E5.12.4.2"),sQuery(id+"F0.wireOp",EDGE,"E5.3.4.3"),sQuery(id+"F0.wireOp",EDGE,"E5.6.4.3"),sQuery(id+"F0.wireOp",EDGE,"E5.9.4.3"),sQuery(id+"F0.wireOp",EDGE,"E5.12.4.3"),sQuery(id+"F0.wireOp",EDGE,"E5.3.4.4"),sQuery(id+"F0.wireOp",EDGE,"E5.6.4.4"),sQuery(id+"F0.wireOp",EDGE,"E5.9.4.4"),sQuery(id+"F0.wireOp",EDGE,"E5.12.4.4"),sQuery(id+"F0.wireOp",EDGE,"E5.3.4.5"),sQuery(id+"F0.wireOp",EDGE,"E5.6.4.5"),sQuery(id+"F0.wireOp",EDGE,"E5.9.4.5"),sQuery(id+"F0.wireOp",EDGE,"E5.12.4.5"),sQuery(id+"F0.wireOp",EDGE,"E5.3.5.1"),sQuery(id+"F0.wireOp",EDGE,"E5.6.5.1"),sQuery(id+"F0.wireOp",EDGE,"E5.9.5.1"),sQuery(id+"F0.wireOp",EDGE,"E5.12.5.1"),sQuery(id+"F0.wireOp",EDGE,"E5.3.5.2"),sQuery(id+"F0.wireOp",EDGE,"E5.6.5.2"),sQuery(id+"F0.wireOp",EDGE,"E5.9.5.2"),sQuery(id+"F0.wireOp",EDGE,"E5.12.5.2"),sQuery(id+"F0.wireOp",EDGE,"E5.3.5.3"),sQuery(id+"F0.wireOp",EDGE,"E5.6.5.3"),sQuery(id+"F0.wireOp",EDGE,"E5.9.5.3"),sQuery(id+"F0.wireOp",EDGE,"E5.12.5.3"),sQuery(id+"F0.wireOp",EDGE,"E5.3.5.4"),sQuery(id+"F0.wireOp",EDGE,"E5.6.5.4"),sQuery(id+"F0.wireOp",EDGE,"E5.9.5.4"),sQuery(id+"F0.wireOp",EDGE,"E5.12.5.4"),sQuery(id+"F0.wireOp",EDGE,"E5.3.5.5"),sQuery(id+"F0.wireOp",EDGE,"E5.6.5.5"),sQuery(id+"F0.wireOp",EDGE,"E5.9.5.5"),sQuery(id+"F0.wireOp",EDGE,"E5.12.5.5"),sQuery(id+"F0.wireOp",EDGE,"E5.3.6.1"),sQuery(id+"F0.wireOp",EDGE,"E5.6.6.1"),sQuery(id+"F0.wireOp",EDGE,"E5.9.6.1"),sQuery(id+"F0.wireOp",EDGE,"E5.12.6.1"),sQuery(id+"F0.wireOp",EDGE,"E5.3.6.2"),sQuery(id+"F0.wireOp",EDGE,"E5.6.6.2"),sQuery(id+"F0.wireOp",EDGE,"E5.9.6.2"),sQuery(id+"F0.wireOp",EDGE,"E5.12.6.2"),sQuery(id+"F0.wireOp",EDGE,"E5.3.6.3"),sQuery(id+"F0.wireOp",EDGE,"E5.6.6.3"),sQuery(id+"F0.wireOp",EDGE,"E5.9.6.3"),sQuery(id+"F0.wireOp",EDGE,"E5.12.6.3"),sQuery(id+"F0.wireOp",EDGE,"E5.3.6.4"),sQuery(id+"F0.wireOp",EDGE,"E5.6.6.4"),sQuery(id+"F0.wireOp",EDGE,"E5.9.6.4"),sQuery(id+"F0.wireOp",EDGE,"E5.12.6.4"),sQuery(id+"F0.wireOp",EDGE,"E5.3.6.5"),sQuery(id+"F0.wireOp",EDGE,"E5.6.6.5"),sQuery(id+"F0.wireOp",EDGE,"E5.9.6.5"),sQuery(id+"F0.wireOp",EDGE,"E5.12.6.5"),sQuery(id+"F0.wireOp",EDGE,"E5.3.7.1"),sQuery(id+"F0.wireOp",EDGE,"E5.6.7.1"),sQuery(id+"F0.wireOp",EDGE,"E5.9.7.1"),sQuery(id+"F0.wireOp",EDGE,"E5.12.7.1"),sQuery(id+"F0.wireOp",EDGE,"E5.3.7.2"),sQuery(id+"F0.wireOp",EDGE,"E5.6.7.2"),sQuery(id+"F0.wireOp",EDGE,"E5.9.7.2"),sQuery(id+"F0.wireOp",EDGE,"E5.12.7.2"),sQuery(id+"F0.wireOp",EDGE,"E5.3.7.3"),sQuery(id+"F0.wireOp",EDGE,"E5.6.7.3"),sQuery(id+"F0.wireOp",EDGE,"E5.9.7.3"),sQuery(id+"F0.wireOp",EDGE,"E5.12.7.3"),sQuery(id+"F0.wireOp",EDGE,"E5.3.7.4"),sQuery(id+"F0.wireOp",EDGE,"E5.6.7.4"),sQuery(id+"F0.wireOp",EDGE,"E5.9.7.4"),sQuery(id+"F0.wireOp",EDGE,"E5.12.7.4"),sQuery(id+"F0.wireOp",EDGE,"E5.3.7.5"),sQuery(id+"F0.wireOp",EDGE,"E5.6.7.5"),sQuery(id+"F0.wireOp",EDGE,"E5.9.7.5"),sQuery(id+"F0.wireOp",EDGE,"E5.12.7.5"),sQuery(id+"F0.wireOp",EDGE,"E5.3.8.1"),sQuery(id+"F0.wireOp",EDGE,"E5.6.8.1"),sQuery(id+"F0.wireOp",EDGE,"E5.9.8.1"),sQuery(id+"F0.wireOp",EDGE,"E5.12.8.1"),sQuery(id+"F0.wireOp",EDGE,"E5.3.8.2"),sQuery(id+"F0.wireOp",EDGE,"E5.6.8.2"),sQuery(id+"F0.wireOp",EDGE,"E5.9.8.2"),sQuery(id+"F0.wireOp",EDGE,"E5.12.8.2"),sQuery(id+"F0.wireOp",EDGE,"E5.3.8.3"),sQuery(id+"F0.wireOp",EDGE,"E5.6.8.3"),sQuery(id+"F0.wireOp",EDGE,"E5.9.8.3"),sQuery(id+"F0.wireOp",EDGE,"E5.12.8.3"),sQuery(id+"F0.wireOp",EDGE,"E5.3.8.4"),sQuery(id+"F0.wireOp",EDGE,"E5.6.8.4"),sQuery(id+"F0.wireOp",EDGE,"E5.9.8.4"),sQuery(id+"F0.wireOp",EDGE,"E5.12.8.4"),sQuery(id+"F0.wireOp",EDGE,"E5.3.8.5"),sQuery(id+"F0.wireOp",EDGE,"E5.6.8.5"),sQuery(id+"F0.wireOp",EDGE,"E5.9.8.5"),sQuery(id+"F0.wireOp",EDGE,"E5.12.8.5"),sQuery(id+"F0.wireOp",EDGE,"E5.3.9.1"),sQuery(id+"F0.wireOp",EDGE,"E5.6.9.1"),sQuery(id+"F0.wireOp",EDGE,"E5.9.9.1"),sQuery(id+"F0.wireOp",EDGE,"E5.12.9.1"),sQuery(id+"F0.wireOp",EDGE,"E5.3.9.2"),sQuery(id+"F0.wireOp",EDGE,"E5.6.9.2"),sQuery(id+"F0.wireOp",EDGE,"E5.9.9.2"),sQuery(id+"F0.wireOp",EDGE,"E5.12.9.2"),sQuery(id+"F0.wireOp",EDGE,"E5.3.9.3"),sQuery(id+"F0.wireOp",EDGE,"E5.6.9.3"),sQuery(id+"F0.wireOp",EDGE,"E5.9.9.3"),sQuery(id+"F0.wireOp",EDGE,"E5.12.9.3"),sQuery(id+"F0.wireOp",EDGE,"E5.3.9.4"),sQuery(id+"F0.wireOp",EDGE,"E5.6.9.4"),sQuery(id+"F0.wireOp",EDGE,"E5.9.9.4"),sQuery(id+"F0.wireOp",EDGE,"E5.12.9.4"),sQuery(id+"F0.wireOp",EDGE,"E5.3.9.5"),sQuery(id+"F0.wireOp",EDGE,"E5.6.9.5"),sQuery(id+"F0.wireOp",EDGE,"E5.9.9.5"),sQuery(id+"F0.wireOp",EDGE,"E5.12.9.5"),sQuery(id+"F0.wireOp",EDGE,"E5.3.10.1"),sQuery(id+"F0.wireOp",EDGE,"E5.6.10.1"),sQuery(id+"F0.wireOp",EDGE,"E5.9.10.1"),sQuery(id+"F0.wireOp",EDGE,"E5.12.10.1"),sQuery(id+"F0.wireOp",EDGE,"E5.3.10.2"),sQuery(id+"F0.wireOp",EDGE,"E5.6.10.2"),sQuery(id+"F0.wireOp",EDGE,"E5.9.10.2"),sQuery(id+"F0.wireOp",EDGE,"E5.12.10.2"),sQuery(id+"F0.wireOp",EDGE,"E5.3.10.3"),sQuery(id+"F0.wireOp",EDGE,"E5.6.10.3"),sQuery(id+"F0.wireOp",EDGE,"E5.9.10.3"),sQuery(id+"F0.wireOp",EDGE,"E5.12.10.3"),sQuery(id+"F0.wireOp",EDGE,"E5.3.10.4"),sQuery(id+"F0.wireOp",EDGE,"E5.6.10.4"),sQuery(id+"F0.wireOp",EDGE,"E5.9.10.4"),sQuery(id+"F0.wireOp",EDGE,"E5.12.10.4"),sQuery(id+"F0.wireOp",EDGE,"E5.3.10.5"),sQuery(id+"F0.wireOp",EDGE,"E5.6.10.5"),sQuery(id+"F0.wireOp",EDGE,"E5.9.10.5"),sQuery(id+"F0.wireOp",EDGE,"E5.12.10.5"),sQuery(id+"F0.wireOp",EDGE,"E5.3.11.1"),sQuery(id+"F0.wireOp",EDGE,"E5.6.11.1"),sQuery(id+"F0.wireOp",EDGE,"E5.9.11.1"),sQuery(id+"F0.wireOp",EDGE,"E5.12.11.1"),sQuery(id+"F0.wireOp",EDGE,"E5.3.11.2"),sQuery(id+"F0.wireOp",EDGE,"E5.6.11.2"),sQuery(id+"F0.wireOp",EDGE,"E5.9.11.2"),sQuery(id+"F0.wireOp",EDGE,"E5.12.11.2"),sQuery(id+"F0.wireOp",EDGE,"E5.3.11.3"),sQuery(id+"F0.wireOp",EDGE,"E5.6.11.3"),sQuery(id+"F0.wireOp",EDGE,"E5.9.11.3"),sQuery(id+"F0.wireOp",EDGE,"E5.12.11.3"),sQuery(id+"F0.wireOp",EDGE,"E5.3.11.4"),sQuery(id+"F0.wireOp",EDGE,"E5.6.11.4"),sQuery(id+"F0.wireOp",EDGE,"E5.9.11.4"),sQuery(id+"F0.wireOp",EDGE,"E5.12.11.4"),sQuery(id+"F0.wireOp",EDGE,"E5.3.11.5"),sQuery(id+"F0.wireOp",EDGE,"E5.6.11.5"),sQuery(id+"F0.wireOp",EDGE,"E5.9.11.5"),sQuery(id+"F0.wireOp",EDGE,"E5.12.11.5"),sQuery(id+"F0.wireOp",EDGE,"E6.bottom"),sQuery(id+"F0.wireOp",EDGE,"E6.top"),sQuery(id+"F0.wireOp",EDGE,"E6.left"),sQuery(id+"F0.wireOp",EDGE,"E6.right"),sQuery(id+"F0.wireOp",EDGE,"E7.0.1.0"),sQuery(id+"F0.wireOp",EDGE,"E7.0.1.1"),sQuery(id+"F0.wireOp",EDGE,"E7.0.1.2"),sQuery(id+"F0.wireOp",EDGE,"E7.0.1.3"),sQuery(id+"F0.wireOp",EDGE,"E7.0.2.0"),sQuery(id+"F0.wireOp",EDGE,"E7.0.2.1"),sQuery(id+"F0.wireOp",EDGE,"E7.0.2.2"),sQuery(id+"F0.wireOp",EDGE,"E7.0.2.3"),sQuery(id+"F0.wireOp",EDGE,"E7.0.3.0"),sQuery(id+"F0.wireOp",EDGE,"E7.0.3.1"),sQuery(id+"F0.wireOp",EDGE,"E7.0.3.2"),sQuery(id+"F0.wireOp",EDGE,"E7.0.3.3"),sQuery(id+"F0.wireOp",EDGE,"E7.0.4.0"),sQuery(id+"F0.wireOp",EDGE,"E7.0.4.1"),sQuery(id+"F0.wireOp",EDGE,"E7.0.4.2"),sQuery(id+"F0.wireOp",EDGE,"E7.0.4.3"),sQuery(id+"F0.wireOp",EDGE,"E7.0.5.0"),sQuery(id+"F0.wireOp",EDGE,"E7.0.5.1"),sQuery(id+"F0.wireOp",EDGE,"E7.0.5.2"),sQuery(id+"F0.wireOp",EDGE,"E7.0.5.3"),sQuery(id+"F0.wireOp",EDGE,"E7.1.0.0"),sQuery(id+"F0.wireOp",EDGE,"E7.1.0.1"),sQuery(id+"F0.wireOp",EDGE,"E7.1.0.2"),sQuery(id+"F0.wireOp",EDGE,"E7.1.0.3"),sQuery(id+"F0.wireOp",EDGE,"E7.1.1.0"),sQuery(id+"F0.wireOp",EDGE,"E7.1.1.1"),sQuery(id+"F0.wireOp",EDGE,"E7.1.1.2"),sQuery(id+"F0.wireOp",EDGE,"E7.1.1.3"),sQuery(id+"F0.wireOp",EDGE,"E7.1.2.0"),sQuery(id+"F0.wireOp",EDGE,"E7.1.2.1"),sQuery(id+"F0.wireOp",EDGE,"E7.1.2.2"),sQuery(id+"F0.wireOp",EDGE,"E7.1.2.3"),sQuery(id+"F0.wireOp",EDGE,"E7.1.3.0"),sQuery(id+"F0.wireOp",EDGE,"E7.1.3.1"),sQuery(id+"F0.wireOp",EDGE,"E7.1.3.2"),sQuery(id+"F0.wireOp",EDGE,"E7.1.3.3"),sQuery(id+"F0.wireOp",EDGE,"E7.1.4.0"),sQuery(id+"F0.wireOp",EDGE,"E7.1.4.1"),sQuery(id+"F0.wireOp",EDGE,"E7.1.4.2"),sQuery(id+"F0.wireOp",EDGE,"E7.1.4.3"),sQuery(id+"F0.wireOp",EDGE,"E7.1.5.0"),sQuery(id+"F0.wireOp",EDGE,"E7.1.5.1"),sQuery(id+"F0.wireOp",EDGE,"E7.1.5.2"),sQuery(id+"F0.wireOp",EDGE,"E7.1.5.3"),sQuery(id+"F0.wireOp",EDGE,"E7.2.0.0"),sQuery(id+"F0.wireOp",EDGE,"E7.2.0.1"),sQuery(id+"F0.wireOp",EDGE,"E7.2.0.2"),sQuery(id+"F0.wireOp",EDGE,"E7.2.0.3"),sQuery(id+"F0.wireOp",EDGE,"E7.2.1.0"),sQuery(id+"F0.wireOp",EDGE,"E7.2.1.1"),sQuery(id+"F0.wireOp",EDGE,"E7.2.1.2"),sQuery(id+"F0.wireOp",EDGE,"E7.2.1.3"),sQuery(id+"F0.wireOp",EDGE,"E7.2.2.0"),sQuery(id+"F0.wireOp",EDGE,"E7.2.2.1"),sQuery(id+"F0.wireOp",EDGE,"E7.2.2.2"),sQuery(id+"F0.wireOp",EDGE,"E7.2.2.3"),sQuery(id+"F0.wireOp",EDGE,"E7.2.3.0"),sQuery(id+"F0.wireOp",EDGE,"E7.2.3.1"),sQuery(id+"F0.wireOp",EDGE,"E7.2.3.2"),sQuery(id+"F0.wireOp",EDGE,"E7.2.3.3"),sQuery(id+"F0.wireOp",EDGE,"E7.2.4.0"),sQuery(id+"F0.wireOp",EDGE,"E7.2.4.1"),sQuery(id+"F0.wireOp",EDGE,"E7.2.4.2"),sQuery(id+"F0.wireOp",EDGE,"E7.2.4.3"),sQuery(id+"F0.wireOp",EDGE,"E7.2.5.0"),sQuery(id+"F0.wireOp",EDGE,"E7.2.5.1"),sQuery(id+"F0.wireOp",EDGE,"E7.2.5.2"),sQuery(id+"F0.wireOp",EDGE,"E7.2.5.3"),sQuery(id+"F0.wireOp",EDGE,"E7.3.0.0"),sQuery(id+"F0.wireOp",EDGE,"E7.3.0.1"),sQuery(id+"F0.wireOp",EDGE,"E7.3.0.2"),sQuery(id+"F0.wireOp",EDGE,"E7.3.0.3"),sQuery(id+"F0.wireOp",EDGE,"E7.3.1.0"),sQuery(id+"F0.wireOp",EDGE,"E7.3.1.1"),sQuery(id+"F0.wireOp",EDGE,"E7.3.1.2"),sQuery(id+"F0.wireOp",EDGE,"E7.3.1.3"),sQuery(id+"F0.wireOp",EDGE,"E7.3.2.0"),sQuery(id+"F0.wireOp",EDGE,"E7.3.2.1"),sQuery(id+"F0.wireOp",EDGE,"E7.3.2.2"),sQuery(id+"F0.wireOp",EDGE,"E7.3.2.3"),sQuery(id+"F0.wireOp",EDGE,"E7.3.3.0"),sQuery(id+"F0.wireOp",EDGE,"E7.3.3.1"),sQuery(id+"F0.wireOp",EDGE,"E7.3.3.2"),sQuery(id+"F0.wireOp",EDGE,"E7.3.3.3"),sQuery(id+"F0.wireOp",EDGE,"E7.3.4.0"),sQuery(id+"F0.wireOp",EDGE,"E7.3.4.1"),sQuery(id+"F0.wireOp",EDGE,"E7.3.4.2"),sQuery(id+"F0.wireOp",EDGE,"E7.3.4.3"),sQuery(id+"F0.wireOp",EDGE,"E7.3.5.0"),sQuery(id+"F0.wireOp",EDGE,"E7.3.5.1"),sQuery(id+"F0.wireOp",EDGE,"E7.3.5.2"),sQuery(id+"F0.wireOp",EDGE,"E7.3.5.3"),sQuery(id+"F0.wireOp",EDGE,"E7.4.0.0"),sQuery(id+"F0.wireOp",EDGE,"E7.4.0.1"),sQuery(id+"F0.wireOp",EDGE,"E7.4.0.2"),sQuery(id+"F0.wireOp",EDGE,"E7.4.0.3"),sQuery(id+"F0.wireOp",EDGE,"E7.4.1.0"),sQuery(id+"F0.wireOp",EDGE,"E7.4.1.1"),sQuery(id+"F0.wireOp",EDGE,"E7.4.1.2"),sQuery(id+"F0.wireOp",EDGE,"E7.4.1.3"),sQuery(id+"F0.wireOp",EDGE,"E7.4.2.0"),sQuery(id+"F0.wireOp",EDGE,"E7.4.2.1"),sQuery(id+"F0.wireOp",EDGE,"E7.4.2.2"),sQuery(id+"F0.wireOp",EDGE,"E7.4.2.3"),sQuery(id+"F0.wireOp",EDGE,"E7.4.3.0"),sQuery(id+"F0.wireOp",EDGE,"E7.4.3.1"),sQuery(id+"F0.wireOp",EDGE,"E7.4.3.2"),sQuery(id+"F0.wireOp",EDGE,"E7.4.3.3"),sQuery(id+"F0.wireOp",EDGE,"E7.4.4.0"),sQuery(id+"F0.wireOp",EDGE,"E7.4.4.1"),sQuery(id+"F0.wireOp",EDGE,"E7.4.4.2"),sQuery(id+"F0.wireOp",EDGE,"E7.4.4.3"),sQuery(id+"F0.wireOp",EDGE,"E7.4.5.0"),sQuery(id+"F0.wireOp",EDGE,"E7.4.5.1"),sQuery(id+"F0.wireOp",EDGE,"E7.4.5.2"),sQuery(id+"F0.wireOp",EDGE,"E7.4.5.3"),sQuery(id+"F0.wireOp",EDGE,"E7.5.0.0"),sQuery(id+"F0.wireOp",EDGE,"E7.5.0.1"),sQuery(id+"F0.wireOp",EDGE,"E7.5.0.2"),sQuery(id+"F0.wireOp",EDGE,"E7.5.0.3"),sQuery(id+"F0.wireOp",EDGE,"E7.5.1.0"),sQuery(id+"F0.wireOp",EDGE,"E7.5.1.1"),sQuery(id+"F0.wireOp",EDGE,"E7.5.1.2"),sQuery(id+"F0.wireOp",EDGE,"E7.5.1.3"),sQuery(id+"F0.wireOp",EDGE,"E7.5.2.0"),sQuery(id+"F0.wireOp",EDGE,"E7.5.2.1"),sQuery(id+"F0.wireOp",EDGE,"E7.5.2.2"),sQuery(id+"F0.wireOp",EDGE,"E7.5.2.3"),sQuery(id+"F0.wireOp",EDGE,"E7.5.3.0"),sQuery(id+"F0.wireOp",EDGE,"E7.5.3.1"),sQuery(id+"F0.wireOp",EDGE,"E7.5.3.2"),sQuery(id+"F0.wireOp",EDGE,"E7.5.3.3"),sQuery(id+"F0.wireOp",EDGE,"E7.5.4.0"),sQuery(id+"F0.wireOp",EDGE,"E7.5.4.1"),sQuery(id+"F0.wireOp",EDGE,"E7.5.4.2"),sQuery(id+"F0.wireOp",EDGE,"E7.5.4.3"),sQuery(id+"F0.wireOp",EDGE,"E7.5.5.0"),sQuery(id+"F0.wireOp",EDGE,"E7.5.5.1"),sQuery(id+"F0.wireOp",EDGE,"E7.5.5.2"),sQuery(id+"F0.wireOp",EDGE,"E7.5.5.3"),sQuery(id+"F0.wireOp",EDGE,"E7.6.0.0"),sQuery(id+"F0.wireOp",EDGE,"E7.6.0.1"),sQuery(id+"F0.wireOp",EDGE,"E7.6.0.2"),sQuery(id+"F0.wireOp",EDGE,"E7.6.0.3"),sQuery(id+"F0.wireOp",EDGE,"E7.6.1.0"),sQuery(id+"F0.wireOp",EDGE,"E7.6.1.1"),sQuery(id+"F0.wireOp",EDGE,"E7.6.1.2"),sQuery(id+"F0.wireOp",EDGE,"E7.6.1.3"),sQuery(id+"F0.wireOp",EDGE,"E7.6.2.0"),sQuery(id+"F0.wireOp",EDGE,"E7.6.2.1"),sQuery(id+"F0.wireOp",EDGE,"E7.6.2.2"),sQuery(id+"F0.wireOp",EDGE,"E7.6.2.3"),sQuery(id+"F0.wireOp",EDGE,"E7.6.3.0"),sQuery(id+"F0.wireOp",EDGE,"E7.6.3.1"),sQuery(id+"F0.wireOp",EDGE,"E7.6.3.2"),sQuery(id+"F0.wireOp",EDGE,"E7.6.3.3"),sQuery(id+"F0.wireOp",EDGE,"E7.6.4.0"),sQuery(id+"F0.wireOp",EDGE,"E7.6.4.1"),sQuery(id+"F0.wireOp",EDGE,"E7.6.4.2"),sQuery(id+"F0.wireOp",EDGE,"E7.6.4.3"),sQuery(id+"F0.wireOp",EDGE,"E7.6.5.0"),sQuery(id+"F0.wireOp",EDGE,"E7.6.5.1"),sQuery(id+"F0.wireOp",EDGE,"E7.6.5.2"),sQuery(id+"F0.wireOp",EDGE,"E7.6.5.3"),sQuery(id+"F0.wireOp",EDGE,"E7.7.0.0"),sQuery(id+"F0.wireOp",EDGE,"E7.7.0.1"),sQuery(id+"F0.wireOp",EDGE,"E7.7.0.2"),sQuery(id+"F0.wireOp",EDGE,"E7.7.0.3"),sQuery(id+"F0.wireOp",EDGE,"E7.7.1.0"),sQuery(id+"F0.wireOp",EDGE,"E7.7.1.1"),sQuery(id+"F0.wireOp",EDGE,"E7.7.1.2"),sQuery(id+"F0.wireOp",EDGE,"E7.7.1.3"),sQuery(id+"F0.wireOp",EDGE,"E7.7.2.0"),sQuery(id+"F0.wireOp",EDGE,"E7.7.2.1"),sQuery(id+"F0.wireOp",EDGE,"E7.7.2.2"),sQuery(id+"F0.wireOp",EDGE,"E7.7.2.3"),sQuery(id+"F0.wireOp",EDGE,"E7.7.3.0"),sQuery(id+"F0.wireOp",EDGE,"E7.7.3.1"),sQuery(id+"F0.wireOp",EDGE,"E7.7.3.2"),sQuery(id+"F0.wireOp",EDGE,"E7.7.3.3"),sQuery(id+"F0.wireOp",EDGE,"E7.7.4.0"),sQuery(id+"F0.wireOp",EDGE,"E7.7.4.1"),sQuery(id+"F0.wireOp",EDGE,"E7.7.4.2"),sQuery(id+"F0.wireOp",EDGE,"E7.7.4.3"),sQuery(id+"F0.wireOp",EDGE,"E7.7.5.0"),sQuery(id+"F0.wireOp",EDGE,"E7.7.5.1"),sQuery(id+"F0.wireOp",EDGE,"E7.7.5.2"),sQuery(id+"F0.wireOp",EDGE,"E7.7.5.3"),sQuery(id+"F0.wireOp",EDGE,"E7.8.0.0"),sQuery(id+"F0.wireOp",EDGE,"E7.8.0.1"),sQuery(id+"F0.wireOp",EDGE,"E7.8.0.2"),sQuery(id+"F0.wireOp",EDGE,"E7.8.0.3"),sQuery(id+"F0.wireOp",EDGE,"E7.8.1.0"),sQuery(id+"F0.wireOp",EDGE,"E7.8.1.1"),sQuery(id+"F0.wireOp",EDGE,"E7.8.1.2"),sQuery(id+"F0.wireOp",EDGE,"E7.8.1.3"),sQuery(id+"F0.wireOp",EDGE,"E7.8.2.0"),sQuery(id+"F0.wireOp",EDGE,"E7.8.2.1"),sQuery(id+"F0.wireOp",EDGE,"E7.8.2.2"),sQuery(id+"F0.wireOp",EDGE,"E7.8.2.3"),sQuery(id+"F0.wireOp",EDGE,"E7.8.3.0"),sQuery(id+"F0.wireOp",EDGE,"E7.8.3.1"),sQuery(id+"F0.wireOp",EDGE,"E7.8.3.2"),sQuery(id+"F0.wireOp",EDGE,"E7.8.3.3"),sQuery(id+"F0.wireOp",EDGE,"E7.8.4.0"),sQuery(id+"F0.wireOp",EDGE,"E7.8.4.1"),sQuery(id+"F0.wireOp",EDGE,"E7.8.4.2"),sQuery(id+"F0.wireOp",EDGE,"E7.8.4.3"),sQuery(id+"F0.wireOp",EDGE,"E7.8.5.0"),sQuery(id+"F0.wireOp",EDGE,"E7.8.5.1"),sQuery(id+"F0.wireOp",EDGE,"E7.8.5.2"),sQuery(id+"F0.wireOp",EDGE,"E7.8.5.3"),sQuery(id+"F0.wireOp",EDGE,"E7.9.0.0"),sQuery(id+"F0.wireOp",EDGE,"E7.9.0.1"),sQuery(id+"F0.wireOp",EDGE,"E7.9.0.2"),sQuery(id+"F0.wireOp",EDGE,"E7.9.0.3"),sQuery(id+"F0.wireOp",EDGE,"E7.9.1.0"),sQuery(id+"F0.wireOp",EDGE,"E7.9.1.1"),sQuery(id+"F0.wireOp",EDGE,"E7.9.1.2"),sQuery(id+"F0.wireOp",EDGE,"E7.9.1.3"),sQuery(id+"F0.wireOp",EDGE,"E7.9.2.0"),sQuery(id+"F0.wireOp",EDGE,"E7.9.2.1"),sQuery(id+"F0.wireOp",EDGE,"E7.9.2.2"),sQuery(id+"F0.wireOp",EDGE,"E7.9.2.3"),sQuery(id+"F0.wireOp",EDGE,"E7.9.3.0"),sQuery(id+"F0.wireOp",EDGE,"E7.9.3.1"),sQuery(id+"F0.wireOp",EDGE,"E7.9.3.2"),sQuery(id+"F0.wireOp",EDGE,"E7.9.3.3"),sQuery(id+"F0.wireOp",EDGE,"E7.9.4.0"),sQuery(id+"F0.wireOp",EDGE,"E7.9.4.1"),sQuery(id+"F0.wireOp",EDGE,"E7.9.4.2"),sQuery(id+"F0.wireOp",EDGE,"E7.9.4.3"),sQuery(id+"F0.wireOp",EDGE,"E7.9.5.0"),sQuery(id+"F0.wireOp",EDGE,"E7.9.5.1"),sQuery(id+"F0.wireOp",EDGE,"E7.9.5.2"),sQuery(id+"F0.wireOp",EDGE,"E7.9.5.3"),sQuery(id+"F0.wireOp",EDGE,"E7.10.0.0"),sQuery(id+"F0.wireOp",EDGE,"E7.10.0.1"),sQuery(id+"F0.wireOp",EDGE,"E7.10.0.2"),sQuery(id+"F0.wireOp",EDGE,"E7.10.0.3"),sQuery(id+"F0.wireOp",EDGE,"E7.10.1.0"),sQuery(id+"F0.wireOp",EDGE,"E7.10.1.1"),sQuery(id+"F0.wireOp",EDGE,"E7.10.1.2"),sQuery(id+"F0.wireOp",EDGE,"E7.10.1.3"),sQuery(id+"F0.wireOp",EDGE,"E7.10.2.0"),sQuery(id+"F0.wireOp",EDGE,"E7.10.2.1"),sQuery(id+"F0.wireOp",EDGE,"E7.10.2.2"),sQuery(id+"F0.wireOp",EDGE,"E7.10.2.3"),sQuery(id+"F0.wireOp",EDGE,"E7.10.3.0"),sQuery(id+"F0.wireOp",EDGE,"E7.10.3.1"),sQuery(id+"F0.wireOp",EDGE,"E7.10.3.2"),sQuery(id+"F0.wireOp",EDGE,"E7.10.3.3"),sQuery(id+"F0.wireOp",EDGE,"E7.10.4.0"),sQuery(id+"F0.wireOp",EDGE,"E7.10.4.1"),sQuery(id+"F0.wireOp",EDGE,"E7.10.4.2"),sQuery(id+"F0.wireOp",EDGE,"E7.10.4.3"),sQuery(id+"F0.wireOp",EDGE,"E7.10.5.0"),sQuery(id+"F0.wireOp",EDGE,"E7.10.5.1"),sQuery(id+"F0.wireOp",EDGE,"E7.10.5.2"),sQuery(id+"F0.wireOp",EDGE,"E7.10.5.3"),sQuery(id+"F0.wireOp",EDGE,"E7.11.0.0"),sQuery(id+"F0.wireOp",EDGE,"E7.11.0.1"),sQuery(id+"F0.wireOp",EDGE,"E7.11.0.2"),sQuery(id+"F0.wireOp",EDGE,"E7.11.0.3"),sQuery(id+"F0.wireOp",EDGE,"E7.11.1.0"),sQuery(id+"F0.wireOp",EDGE,"E7.11.1.1"),sQuery(id+"F0.wireOp",EDGE,"E7.11.1.2"),sQuery(id+"F0.wireOp",EDGE,"E7.11.1.3"),sQuery(id+"F0.wireOp",EDGE,"E7.11.2.0"),sQuery(id+"F0.wireOp",EDGE,"E7.11.2.1"),sQuery(id+"F0.wireOp",EDGE,"E7.11.2.2"),sQuery(id+"F0.wireOp",EDGE,"E7.11.2.3"),sQuery(id+"F0.wireOp",EDGE,"E7.11.3.0"),sQuery(id+"F0.wireOp",EDGE,"E7.11.3.1"),sQuery(id+"F0.wireOp",EDGE,"E7.11.3.2"),sQuery(id+"F0.wireOp",EDGE,"E7.11.3.3"),sQuery(id+"F0.wireOp",EDGE,"E7.11.4.0"),sQuery(id+"F0.wireOp",EDGE,"E7.11.4.1"),sQuery(id+"F0.wireOp",EDGE,"E7.11.4.2"),sQuery(id+"F0.wireOp",EDGE,"E7.11.4.3"),sQuery(id+"F0.wireOp",EDGE,"E7.11.5.0"),sQuery(id+"F0.wireOp",EDGE,"E7.11.5.1"),sQuery(id+"F0.wireOp",EDGE,"E7.11.5.2"),sQuery(id+"F0.wireOp",EDGE,"E7.11.5.3")])],"isStart":false});
            var sketch = newSketch(context, id + "F2", { "sketchPlane" : qUnion([Q0, Q1])});
            skLineSegment(sketch, "E8.bottom", {"start": v(-129.55, 153.24) * mm, "end": v(-123.55, 153.24) * mm});
            skLineSegment(sketch, "E8.top", {"start": v(-129.55, 147.24) * mm, "end": v(-123.55, 147.24) * mm});
            skLineSegment(sketch, "E8.left", {"start": v(-129.55, 153.24) * mm, "end": v(-129.55, 147.24) * mm});
            skLineSegment(sketch, "E8.right", {"start": v(-123.55, 153.24) * mm, "end": v(-123.55, 147.24) * mm});
            skLineSegment(sketch, "E9.bottom", {"start": v(104.45, 153.24) * mm, "end": v(98.45, 153.24) * mm});
            skLineSegment(sketch, "E9.top", {"start": v(104.45, 147.24) * mm, "end": v(98.45, 147.24) * mm});
            skLineSegment(sketch, "E9.left", {"start": v(104.45, 153.24) * mm, "end": v(104.45, 147.24) * mm});
            skLineSegment(sketch, "E9.right", {"start": v(98.45, 153.24) * mm, "end": v(98.45, 147.24) * mm});
            skLineSegment(sketch, "E10.bottom", {"start": v(104.45, -80.76) * mm, "end": v(98.45, -80.76) * mm});
            skLineSegment(sketch, "E10.top", {"start": v(104.45, -74.76) * mm, "end": v(98.45, -74.76) * mm});
            skLineSegment(sketch, "E10.left", {"start": v(104.45, -80.76) * mm, "end": v(104.45, -74.76) * mm});
            skLineSegment(sketch, "E10.right", {"start": v(98.45, -80.76) * mm, "end": v(98.45, -74.76) * mm});
            skLineSegment(sketch, "E11.bottom", {"start": v(-129.55, -80.76) * mm, "end": v(-123.55, -80.76) * mm});
            skLineSegment(sketch, "E11.top", {"start": v(-129.55, -74.76) * mm, "end": v(-123.55, -74.76) * mm});
            skLineSegment(sketch, "E11.left", {"start": v(-129.55, -80.76) * mm, "end": v(-129.55, -74.76) * mm});
            skLineSegment(sketch, "E11.right", {"start": v(-123.55, -80.76) * mm, "end": v(-123.55, -74.76) * mm});
            skSolve(sketch);
        }
        {
            var Q0;
            Q0=makeQuery(id+"F2.imprint","IMPRINT",FACE,{"disambiguationData":[TD([[makeQuery(id+"F2.imprint","IMPRINT",EDGE,{"derivedFrom":sQuery(id+"F2.wireOp",EDGE,"E8.bottom")}),-1.0]])]});
            var Q1;
            Q1=makeQuery(id+"F2.imprint","IMPRINT",FACE,{"disambiguationData":[TD([[makeQuery(id+"F2.imprint","IMPRINT",EDGE,{"derivedFrom":sQuery(id+"F2.wireOp",EDGE,"E9.bottom")}),1.0]])]});
            var Q2;
            Q2=makeQuery(id+"F2.imprint","IMPRINT",FACE,{"disambiguationData":[TD([[makeQuery(id+"F2.imprint","IMPRINT",EDGE,{"derivedFrom":sQuery(id+"F2.wireOp",EDGE,"E10.bottom")}),-1.0]])]});
            var Q3;
            Q3=makeQuery(id+"F2.imprint","IMPRINT",FACE,{"disambiguationData":[TD([[makeQuery(id+"F2.imprint","IMPRINT",EDGE,{"derivedFrom":sQuery(id+"F2.wireOp",EDGE,"E11.bottom")}),1.0]])]});
            extrude(context, id + "F3", {"entities" : qUnion([Q0, Q1, Q2, Q3]), "operationType" : NewBodyOperationType.REMOVE, "endBound" : BoundingType.THROUGH_ALL, "oppositeDirection" : true, "depth" : 25 * mm});
        }
    });
